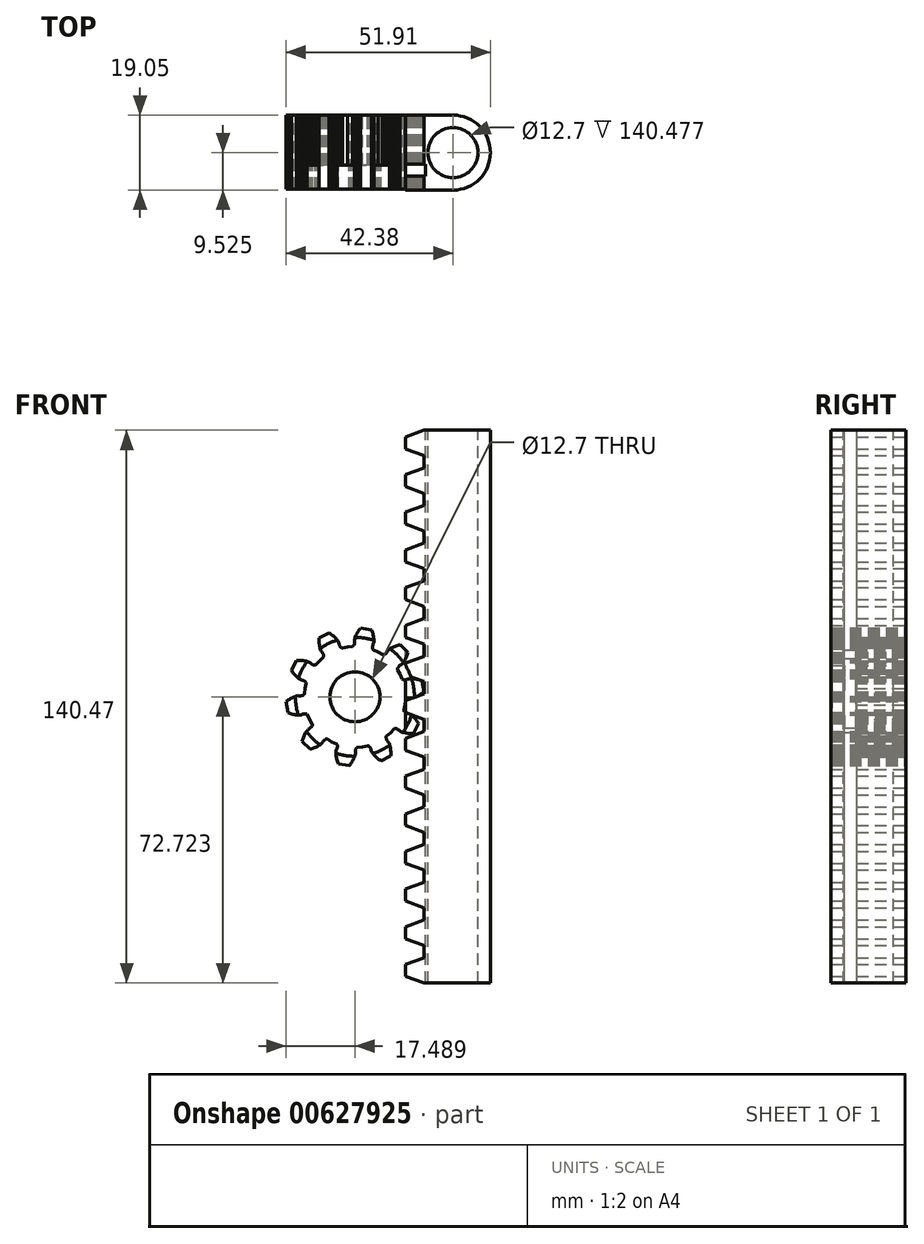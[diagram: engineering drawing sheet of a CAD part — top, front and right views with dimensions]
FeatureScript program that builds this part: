
annotation { "Feature Type Name" : "Feature", "Feature Type Description" : "" }
export const myFeature = defineFeature(function(context is Context, id is Id, definition is map)
    precondition{}
    {
        {
            var Q0;
            Q0=qCreatedBy(makeId("Front.planeOp"),FACE);
            var sketch = newSketch(context, id + "F0", { "sketchPlane" : qUnion([Q0])});
            skLineSegment(sketch, "E0", {"start": v(-42.72, 2.41) * mm, "end": v(-42.7, 2.18) * mm});
            skLineSegment(sketch, "E1", {"start": v(-42.7, 2.18) * mm, "end": v(-42.65, 2.08) * mm});
            skLineSegment(sketch, "E2", {"start": v(-42.65, 2.08) * mm, "end": v(-42.6, 2) * mm});
            skLineSegment(sketch, "E3", {"start": v(-42.6, 2) * mm, "end": v(-42.53, 1.93) * mm});
            skLineSegment(sketch, "E4", {"start": v(-42.53, 1.93) * mm, "end": v(-42.47, 1.88) * mm});
            skLineSegment(sketch, "E5", {"start": v(-42.47, 1.88) * mm, "end": v(-42.34, 1.78) * mm});
            skLineSegment(sketch, "E6", {"start": v(-42.34, 1.78) * mm, "end": v(-42.2, 1.7) * mm});
            skLineSegment(sketch, "E7", {"start": v(-42.2, 1.7) * mm, "end": v(-42.06, 1.63) * mm});
            skLineSegment(sketch, "E8", {"start": v(-42.06, 1.63) * mm, "end": v(-41.9, 1.57) * mm});
            skLineSegment(sketch, "E9", {"start": v(-41.9, 1.57) * mm, "end": v(-41.61, 1.48) * mm});
            skLineSegment(sketch, "E10", {"start": v(-41.61, 1.48) * mm, "end": v(-41.31, 1.38) * mm});
            skLineSegment(sketch, "E11", {"start": v(-41.31, 1.38) * mm, "end": v(-41.04, 1.22) * mm});
            skLineSegment(sketch, "E12", {"start": v(-41.04, 1.22) * mm, "end": v(-40.77, 1.04) * mm});
            skLineSegment(sketch, "E13", {"start": v(-40.77, 1.04) * mm, "end": v(-40.5, 0.83) * mm});
            skLineSegment(sketch, "E14", {"start": v(-40.5, 0.83) * mm, "end": v(-40.26, 0.6) * mm});
            skLineSegment(sketch, "E15", {"start": v(-40.26, 0.6) * mm, "end": v(-40.01, 0.35) * mm});
            skLineSegment(sketch, "E16", {"start": v(-40.01, 0.35) * mm, "end": v(-39.77, 0.1) * mm});
            skLineSegment(sketch, "E17", {"start": v(-39.77, 0.1) * mm, "end": v(-39.54, -0.19) * mm});
            skLineSegment(sketch, "E18", {"start": v(-39.54, -0.19) * mm, "end": v(-39.32, -0.48) * mm});
            skLineSegment(sketch, "E19", {"start": v(-39.32, -0.48) * mm, "end": v(-39.1, -0.79) * mm});
            skLineSegment(sketch, "E20", {"start": v(-39.1, -0.79) * mm, "end": v(-38.95, -1.03) * mm});
            skLineSegment(sketch, "E21", {"start": v(-38.95, -1.03) * mm, "end": v(-40.25, -3.53) * mm});
            skLineSegment(sketch, "E22", {"start": v(-40.25, -3.53) * mm, "end": v(-40.53, -3.54) * mm});
            skLineSegment(sketch, "E23", {"start": v(-40.53, -3.54) * mm, "end": v(-40.9, -3.55) * mm});
            skLineSegment(sketch, "E24", {"start": v(-40.9, -3.55) * mm, "end": v(-41.28, -3.53) * mm});
            skLineSegment(sketch, "E25", {"start": v(-41.28, -3.53) * mm, "end": v(-41.63, -3.5) * mm});
            skLineSegment(sketch, "E26", {"start": v(-41.63, -3.5) * mm, "end": v(-41.99, -3.46) * mm});
            skLineSegment(sketch, "E27", {"start": v(-41.99, -3.46) * mm, "end": v(-42.33, -3.4) * mm});
            skLineSegment(sketch, "E28", {"start": v(-42.33, -3.4) * mm, "end": v(-42.66, -3.33) * mm});
            skLineSegment(sketch, "E29", {"start": v(-42.66, -3.33) * mm, "end": v(-42.98, -3.24) * mm});
            skLineSegment(sketch, "E30", {"start": v(-42.98, -3.24) * mm, "end": v(-43.29, -3.13) * mm});
            skLineSegment(sketch, "E31", {"start": v(-43.29, -3.13) * mm, "end": v(-43.58, -3) * mm});
            skLineSegment(sketch, "E32", {"start": v(-43.58, -3) * mm, "end": v(-43.83, -2.8) * mm});
            skLineSegment(sketch, "E33", {"start": v(-43.83, -2.8) * mm, "end": v(-44.08, -2.62) * mm});
            skLineSegment(sketch, "E34", {"start": v(-44.08, -2.62) * mm, "end": v(-44.2, -2.53) * mm});
            skLineSegment(sketch, "E35", {"start": v(-44.2, -2.53) * mm, "end": v(-44.35, -2.45) * mm});
            skLineSegment(sketch, "E36", {"start": v(-44.35, -2.45) * mm, "end": v(-44.5, -2.39) * mm});
            skLineSegment(sketch, "E37", {"start": v(-44.5, -2.39) * mm, "end": v(-44.65, -2.34) * mm});
            skLineSegment(sketch, "E38", {"start": v(-44.65, -2.34) * mm, "end": v(-44.73, -2.32) * mm});
            skLineSegment(sketch, "E39", {"start": v(-44.73, -2.32) * mm, "end": v(-44.82, -2.3) * mm});
            skLineSegment(sketch, "E40", {"start": v(-44.82, -2.3) * mm, "end": v(-44.92, -2.3) * mm});
            skLineSegment(sketch, "E41", {"start": v(-44.92, -2.3) * mm, "end": v(-45.03, -2.32) * mm});
            skLineSegment(sketch, "E42", {"start": v(-45.03, -2.32) * mm, "end": v(-45.23, -2.44) * mm});
            skLineSegment(sketch, "E43", {"start": v(-45.23, -2.44) * mm, "end": v(-46.1, -3.38) * mm});
            skLineSegment(sketch, "E44", {"start": v(-46.1, -3.38) * mm, "end": v(-47.05, -4.24) * mm});
            skLineSegment(sketch, "E45", {"start": v(-47.05, -4.24) * mm, "end": v(-47.18, -4.44) * mm});
            skLineSegment(sketch, "E46", {"start": v(-47.18, -4.44) * mm, "end": v(-47.2, -4.55) * mm});
            skLineSegment(sketch, "E47", {"start": v(-47.2, -4.55) * mm, "end": v(-47.2, -4.65) * mm});
            skLineSegment(sketch, "E48", {"start": v(-47.2, -4.65) * mm, "end": v(-47.18, -4.74) * mm});
            skLineSegment(sketch, "E49", {"start": v(-47.18, -4.74) * mm, "end": v(-47.16, -4.82) * mm});
            skLineSegment(sketch, "E50", {"start": v(-47.16, -4.82) * mm, "end": v(-47.11, -4.98) * mm});
            skLineSegment(sketch, "E51", {"start": v(-47.11, -4.98) * mm, "end": v(-47.05, -5.13) * mm});
            skLineSegment(sketch, "E52", {"start": v(-47.05, -5.13) * mm, "end": v(-46.98, -5.26) * mm});
            skLineSegment(sketch, "E53", {"start": v(-46.98, -5.26) * mm, "end": v(-46.9, -5.4) * mm});
            skLineSegment(sketch, "E54", {"start": v(-46.9, -5.4) * mm, "end": v(-46.7, -5.65) * mm});
            skLineSegment(sketch, "E55", {"start": v(-46.7, -5.65) * mm, "end": v(-46.52, -5.9) * mm});
            skLineSegment(sketch, "E56", {"start": v(-46.52, -5.9) * mm, "end": v(-46.39, -6.2) * mm});
            skLineSegment(sketch, "E57", {"start": v(-46.39, -6.2) * mm, "end": v(-46.28, -6.5) * mm});
            skLineSegment(sketch, "E58", {"start": v(-46.28, -6.5) * mm, "end": v(-46.2, -6.82) * mm});
            skLineSegment(sketch, "E59", {"start": v(-46.2, -6.82) * mm, "end": v(-46.12, -7.15) * mm});
            skLineSegment(sketch, "E60", {"start": v(-46.12, -7.15) * mm, "end": v(-46.07, -7.5) * mm});
            skLineSegment(sketch, "E61", {"start": v(-46.07, -7.5) * mm, "end": v(-46.03, -7.85) * mm});
            skLineSegment(sketch, "E62", {"start": v(-46.03, -7.85) * mm, "end": v(-46, -8.2) * mm});
            skLineSegment(sketch, "E63", {"start": v(-46, -8.2) * mm, "end": v(-46, -8.58) * mm});
            skLineSegment(sketch, "E64", {"start": v(-46, -8.58) * mm, "end": v(-46.01, -8.95) * mm});
            skLineSegment(sketch, "E65", {"start": v(-46.01, -8.95) * mm, "end": v(-46.03, -9.24) * mm});
            skLineSegment(sketch, "E66", {"start": v(-46.03, -9.24) * mm, "end": v(-48.55, -10.5) * mm});
            skLineSegment(sketch, "E67", {"start": v(-48.55, -10.5) * mm, "end": v(-48.78, -10.34) * mm});
            skLineSegment(sketch, "E68", {"start": v(-48.78, -10.34) * mm, "end": v(-49.09, -10.12) * mm});
            skLineSegment(sketch, "E69", {"start": v(-49.09, -10.12) * mm, "end": v(-49.38, -9.9) * mm});
            skLineSegment(sketch, "E70", {"start": v(-49.38, -9.9) * mm, "end": v(-49.65, -9.67) * mm});
            skLineSegment(sketch, "E71", {"start": v(-49.65, -9.67) * mm, "end": v(-49.91, -9.42) * mm});
            skLineSegment(sketch, "E72", {"start": v(-49.91, -9.42) * mm, "end": v(-50.16, -9.18) * mm});
            skLineSegment(sketch, "E73", {"start": v(-50.16, -9.18) * mm, "end": v(-50.38, -8.92) * mm});
            skLineSegment(sketch, "E74", {"start": v(-50.38, -8.92) * mm, "end": v(-50.59, -8.66) * mm});
            skLineSegment(sketch, "E75", {"start": v(-50.59, -8.66) * mm, "end": v(-50.77, -8.39) * mm});
            skLineSegment(sketch, "E76", {"start": v(-50.77, -8.39) * mm, "end": v(-50.92, -8.1) * mm});
            skLineSegment(sketch, "E77", {"start": v(-50.92, -8.1) * mm, "end": v(-51.02, -7.8) * mm});
            skLineSegment(sketch, "E78", {"start": v(-51.02, -7.8) * mm, "end": v(-51.1, -7.51) * mm});
            skLineSegment(sketch, "E79", {"start": v(-51.1, -7.51) * mm, "end": v(-51.16, -7.36) * mm});
            skLineSegment(sketch, "E80", {"start": v(-51.16, -7.36) * mm, "end": v(-51.23, -7.22) * mm});
            skLineSegment(sketch, "E81", {"start": v(-51.23, -7.22) * mm, "end": v(-51.3, -7.08) * mm});
            skLineSegment(sketch, "E82", {"start": v(-51.3, -7.08) * mm, "end": v(-51.4, -6.95) * mm});
            skLineSegment(sketch, "E83", {"start": v(-51.4, -6.95) * mm, "end": v(-51.46, -6.88) * mm});
            skLineSegment(sketch, "E84", {"start": v(-51.46, -6.88) * mm, "end": v(-51.53, -6.82) * mm});
            skLineSegment(sketch, "E85", {"start": v(-51.53, -6.82) * mm, "end": v(-51.6, -6.76) * mm});
            skLineSegment(sketch, "E86", {"start": v(-51.6, -6.76) * mm, "end": v(-51.7, -6.7) * mm});
            skLineSegment(sketch, "E87", {"start": v(-51.7, -6.7) * mm, "end": v(-51.94, -6.69) * mm});
            skLineSegment(sketch, "E88", {"start": v(-51.94, -6.69) * mm, "end": v(-53.2, -6.94) * mm});
            skLineSegment(sketch, "E89", {"start": v(-53.2, -6.94) * mm, "end": v(-54.47, -7.07) * mm});
            skLineSegment(sketch, "E90", {"start": v(-54.47, -7.07) * mm, "end": v(-54.68, -7.16) * mm});
            skLineSegment(sketch, "E91", {"start": v(-54.68, -7.16) * mm, "end": v(-54.76, -7.24) * mm});
            skLineSegment(sketch, "E92", {"start": v(-54.76, -7.24) * mm, "end": v(-54.82, -7.32) * mm});
            skLineSegment(sketch, "E93", {"start": v(-54.82, -7.32) * mm, "end": v(-54.86, -7.4) * mm});
            skLineSegment(sketch, "E94", {"start": v(-54.86, -7.4) * mm, "end": v(-54.9, -7.48) * mm});
            skLineSegment(sketch, "E95", {"start": v(-54.9, -7.48) * mm, "end": v(-54.95, -7.64) * mm});
            skLineSegment(sketch, "E96", {"start": v(-54.95, -7.64) * mm, "end": v(-54.99, -7.8) * mm});
            skLineSegment(sketch, "E97", {"start": v(-54.99, -7.8) * mm, "end": v(-55, -7.95) * mm});
            skLineSegment(sketch, "E98", {"start": v(-55, -7.95) * mm, "end": v(-55.02, -8.1) * mm});
            skLineSegment(sketch, "E99", {"start": v(-55.02, -8.1) * mm, "end": v(-55.01, -8.42) * mm});
            skLineSegment(sketch, "E100", {"start": v(-55.01, -8.42) * mm, "end": v(-55.01, -8.73) * mm});
            skLineSegment(sketch, "E101", {"start": v(-55.01, -8.73) * mm, "end": v(-55.08, -9.04) * mm});
            skLineSegment(sketch, "E102", {"start": v(-55.08, -9.04) * mm, "end": v(-55.17, -9.36) * mm});
            skLineSegment(sketch, "E103", {"start": v(-55.17, -9.36) * mm, "end": v(-55.3, -9.67) * mm});
            skLineSegment(sketch, "E104", {"start": v(-55.3, -9.67) * mm, "end": v(-55.43, -9.98) * mm});
            skLineSegment(sketch, "E105", {"start": v(-55.43, -9.98) * mm, "end": v(-55.59, -10.29) * mm});
            skLineSegment(sketch, "E106", {"start": v(-55.59, -10.29) * mm, "end": v(-55.76, -10.6) * mm});
            skLineSegment(sketch, "E107", {"start": v(-55.76, -10.6) * mm, "end": v(-55.96, -10.9) * mm});
            skLineSegment(sketch, "E108", {"start": v(-55.96, -10.9) * mm, "end": v(-56.17, -11.2) * mm});
            skLineSegment(sketch, "E109", {"start": v(-56.17, -11.2) * mm, "end": v(-56.4, -11.5) * mm});
            skLineSegment(sketch, "E110", {"start": v(-56.4, -11.5) * mm, "end": v(-56.57, -11.72) * mm});
            skLineSegment(sketch, "E111", {"start": v(-56.57, -11.72) * mm, "end": v(-59.35, -11.26) * mm});
            skLineSegment(sketch, "E112", {"start": v(-59.35, -11.26) * mm, "end": v(-59.45, -11) * mm});
            skLineSegment(sketch, "E113", {"start": v(-59.45, -11) * mm, "end": v(-59.57, -10.64) * mm});
            skLineSegment(sketch, "E114", {"start": v(-59.57, -10.64) * mm, "end": v(-59.67, -10.29) * mm});
            skLineSegment(sketch, "E115", {"start": v(-59.67, -10.29) * mm, "end": v(-59.76, -9.93) * mm});
            skLineSegment(sketch, "E116", {"start": v(-59.76, -9.93) * mm, "end": v(-59.83, -9.59) * mm});
            skLineSegment(sketch, "E117", {"start": v(-59.83, -9.59) * mm, "end": v(-59.88, -9.24) * mm});
            skLineSegment(sketch, "E118", {"start": v(-59.88, -9.24) * mm, "end": v(-59.91, -8.9) * mm});
            skLineSegment(sketch, "E119", {"start": v(-59.91, -8.9) * mm, "end": v(-59.92, -8.57) * mm});
            skLineSegment(sketch, "E120", {"start": v(-59.92, -8.57) * mm, "end": v(-59.91, -8.25) * mm});
            skLineSegment(sketch, "E121", {"start": v(-59.91, -8.25) * mm, "end": v(-59.87, -7.93) * mm});
            skLineSegment(sketch, "E122", {"start": v(-59.87, -7.93) * mm, "end": v(-59.77, -7.63) * mm});
            skLineSegment(sketch, "E123", {"start": v(-59.77, -7.63) * mm, "end": v(-59.67, -7.34) * mm});
            skLineSegment(sketch, "E124", {"start": v(-59.67, -7.34) * mm, "end": v(-59.63, -7.19) * mm});
            skLineSegment(sketch, "E125", {"start": v(-59.63, -7.19) * mm, "end": v(-59.6, -7.03) * mm});
            skLineSegment(sketch, "E126", {"start": v(-59.6, -7.03) * mm, "end": v(-59.58, -6.87) * mm});
            skLineSegment(sketch, "E127", {"start": v(-59.58, -6.87) * mm, "end": v(-59.58, -6.7) * mm});
            skLineSegment(sketch, "E128", {"start": v(-59.58, -6.7) * mm, "end": v(-59.59, -6.62) * mm});
            skLineSegment(sketch, "E129", {"start": v(-59.59, -6.62) * mm, "end": v(-59.6, -6.53) * mm});
            skLineSegment(sketch, "E130", {"start": v(-59.6, -6.53) * mm, "end": v(-59.63, -6.44) * mm});
            skLineSegment(sketch, "E131", {"start": v(-59.63, -6.44) * mm, "end": v(-59.68, -6.34) * mm});
            skLineSegment(sketch, "E132", {"start": v(-59.68, -6.34) * mm, "end": v(-59.86, -6.18) * mm});
            skLineSegment(sketch, "E133", {"start": v(-59.86, -6.18) * mm, "end": v(-61.02, -5.65) * mm});
            skLineSegment(sketch, "E134", {"start": v(-61.02, -5.65) * mm, "end": v(-62.13, -5) * mm});
            skLineSegment(sketch, "E135", {"start": v(-62.13, -5) * mm, "end": v(-62.36, -4.95) * mm});
            skLineSegment(sketch, "E136", {"start": v(-62.36, -4.95) * mm, "end": v(-62.47, -4.97) * mm});
            skLineSegment(sketch, "E137", {"start": v(-62.47, -4.97) * mm, "end": v(-62.56, -5) * mm});
            skLineSegment(sketch, "E138", {"start": v(-62.56, -5) * mm, "end": v(-62.64, -5.04) * mm});
            skLineSegment(sketch, "E139", {"start": v(-62.64, -5.04) * mm, "end": v(-62.72, -5.08) * mm});
            skLineSegment(sketch, "E140", {"start": v(-62.72, -5.08) * mm, "end": v(-62.85, -5.18) * mm});
            skLineSegment(sketch, "E141", {"start": v(-62.85, -5.18) * mm, "end": v(-62.97, -5.28) * mm});
            skLineSegment(sketch, "E142", {"start": v(-62.97, -5.28) * mm, "end": v(-63.08, -5.4) * mm});
            skLineSegment(sketch, "E143", {"start": v(-63.08, -5.4) * mm, "end": v(-63.18, -5.52) * mm});
            skLineSegment(sketch, "E144", {"start": v(-63.18, -5.52) * mm, "end": v(-63.36, -5.77) * mm});
            skLineSegment(sketch, "E145", {"start": v(-63.36, -5.77) * mm, "end": v(-63.55, -6.03) * mm});
            skLineSegment(sketch, "E146", {"start": v(-63.55, -6.03) * mm, "end": v(-63.78, -6.24) * mm});
            skLineSegment(sketch, "E147", {"start": v(-63.78, -6.24) * mm, "end": v(-64.04, -6.44) * mm});
            skLineSegment(sketch, "E148", {"start": v(-64.04, -6.44) * mm, "end": v(-64.32, -6.62) * mm});
            skLineSegment(sketch, "E149", {"start": v(-64.32, -6.62) * mm, "end": v(-64.62, -6.8) * mm});
            skLineSegment(sketch, "E150", {"start": v(-64.62, -6.8) * mm, "end": v(-64.93, -6.95) * mm});
            skLineSegment(sketch, "E151", {"start": v(-64.93, -6.95) * mm, "end": v(-65.25, -7.1) * mm});
            skLineSegment(sketch, "E152", {"start": v(-65.25, -7.1) * mm, "end": v(-65.58, -7.23) * mm});
            skLineSegment(sketch, "E153", {"start": v(-65.58, -7.23) * mm, "end": v(-65.93, -7.35) * mm});
            skLineSegment(sketch, "E154", {"start": v(-65.93, -7.35) * mm, "end": v(-66.3, -7.46) * mm});
            skLineSegment(sketch, "E155", {"start": v(-66.3, -7.46) * mm, "end": v(-66.57, -7.53) * mm});
            skLineSegment(sketch, "E156", {"start": v(-66.57, -7.53) * mm, "end": v(-68.55, -5.52) * mm});
            skLineSegment(sketch, "E157", {"start": v(-68.55, -5.52) * mm, "end": v(-68.47, -5.25) * mm});
            skLineSegment(sketch, "E158", {"start": v(-68.47, -5.25) * mm, "end": v(-68.36, -4.9) * mm});
            skLineSegment(sketch, "E159", {"start": v(-68.36, -4.9) * mm, "end": v(-68.23, -4.55) * mm});
            skLineSegment(sketch, "E160", {"start": v(-68.23, -4.55) * mm, "end": v(-68.1, -4.21) * mm});
            skLineSegment(sketch, "E161", {"start": v(-68.1, -4.21) * mm, "end": v(-67.95, -3.9) * mm});
            skLineSegment(sketch, "E162", {"start": v(-67.95, -3.9) * mm, "end": v(-67.79, -3.58) * mm});
            skLineSegment(sketch, "E163", {"start": v(-67.79, -3.58) * mm, "end": v(-67.61, -3.3) * mm});
            skLineSegment(sketch, "E164", {"start": v(-67.61, -3.3) * mm, "end": v(-67.43, -3.01) * mm});
            skLineSegment(sketch, "E165", {"start": v(-67.43, -3.01) * mm, "end": v(-67.23, -2.76) * mm});
            skLineSegment(sketch, "E166", {"start": v(-67.23, -2.76) * mm, "end": v(-67, -2.52) * mm});
            skLineSegment(sketch, "E167", {"start": v(-67, -2.52) * mm, "end": v(-66.75, -2.34) * mm});
            skLineSegment(sketch, "E168", {"start": v(-66.75, -2.34) * mm, "end": v(-66.5, -2.17) * mm});
            skLineSegment(sketch, "E169", {"start": v(-66.5, -2.17) * mm, "end": v(-66.37, -2.07) * mm});
            skLineSegment(sketch, "E170", {"start": v(-66.37, -2.07) * mm, "end": v(-66.26, -1.96) * mm});
            skLineSegment(sketch, "E171", {"start": v(-66.26, -1.96) * mm, "end": v(-66.15, -1.84) * mm});
            skLineSegment(sketch, "E172", {"start": v(-66.15, -1.84) * mm, "end": v(-66.05, -1.7) * mm});
            skLineSegment(sketch, "E173", {"start": v(-66.05, -1.7) * mm, "end": v(-66, -1.63) * mm});
            skLineSegment(sketch, "E174", {"start": v(-66, -1.63) * mm, "end": v(-65.97, -1.55) * mm});
            skLineSegment(sketch, "E175", {"start": v(-65.97, -1.55) * mm, "end": v(-65.94, -1.46) * mm});
            skLineSegment(sketch, "E176", {"start": v(-65.94, -1.46) * mm, "end": v(-65.92, -1.35) * mm});
            skLineSegment(sketch, "E177", {"start": v(-65.92, -1.35) * mm, "end": v(-65.97, -1.12) * mm});
            skLineSegment(sketch, "E178", {"start": v(-65.97, -1.12) * mm, "end": v(-66.6, 0) * mm});
            skLineSegment(sketch, "E179", {"start": v(-66.6, 0) * mm, "end": v(-67.12, 1.17) * mm});
            skLineSegment(sketch, "E180", {"start": v(-67.12, 1.17) * mm, "end": v(-67.27, 1.35) * mm});
            skLineSegment(sketch, "E181", {"start": v(-67.27, 1.35) * mm, "end": v(-67.37, 1.4) * mm});
            skLineSegment(sketch, "E182", {"start": v(-67.37, 1.4) * mm, "end": v(-67.46, 1.43) * mm});
            skLineSegment(sketch, "E183", {"start": v(-67.46, 1.43) * mm, "end": v(-67.55, 1.44) * mm});
            skLineSegment(sketch, "E184", {"start": v(-67.55, 1.44) * mm, "end": v(-67.64, 1.45) * mm});
            skLineSegment(sketch, "E185", {"start": v(-67.64, 1.45) * mm, "end": v(-67.8, 1.45) * mm});
            skLineSegment(sketch, "E186", {"start": v(-67.8, 1.45) * mm, "end": v(-67.96, 1.44) * mm});
            skLineSegment(sketch, "E187", {"start": v(-67.96, 1.44) * mm, "end": v(-68.12, 1.41) * mm});
            skLineSegment(sketch, "E188", {"start": v(-68.12, 1.41) * mm, "end": v(-68.27, 1.37) * mm});
            skLineSegment(sketch, "E189", {"start": v(-68.27, 1.37) * mm, "end": v(-68.57, 1.27) * mm});
            skLineSegment(sketch, "E190", {"start": v(-68.57, 1.27) * mm, "end": v(-68.86, 1.18) * mm});
            skLineSegment(sketch, "E191", {"start": v(-68.86, 1.18) * mm, "end": v(-69.18, 1.14) * mm});
            skLineSegment(sketch, "E192", {"start": v(-69.18, 1.14) * mm, "end": v(-69.5, 1.13) * mm});
            skLineSegment(sketch, "E193", {"start": v(-69.5, 1.13) * mm, "end": v(-69.84, 1.15) * mm});
            skLineSegment(sketch, "E194", {"start": v(-69.84, 1.15) * mm, "end": v(-70.18, 1.18) * mm});
            skLineSegment(sketch, "E195", {"start": v(-70.18, 1.18) * mm, "end": v(-70.52, 1.24) * mm});
            skLineSegment(sketch, "E196", {"start": v(-70.52, 1.24) * mm, "end": v(-70.87, 1.31) * mm});
            skLineSegment(sketch, "E197", {"start": v(-70.87, 1.31) * mm, "end": v(-71.22, 1.4) * mm});
            skLineSegment(sketch, "E198", {"start": v(-71.22, 1.4) * mm, "end": v(-71.57, 1.5) * mm});
            skLineSegment(sketch, "E199", {"start": v(-71.57, 1.5) * mm, "end": v(-71.92, 1.63) * mm});
            skLineSegment(sketch, "E200", {"start": v(-71.92, 1.63) * mm, "end": v(-72.19, 1.74) * mm});
            skLineSegment(sketch, "E201", {"start": v(-72.19, 1.74) * mm, "end": v(-72.61, 4.52) * mm});
            skLineSegment(sketch, "E202", {"start": v(-72.61, 4.52) * mm, "end": v(-72.39, 4.7) * mm});
            skLineSegment(sketch, "E203", {"start": v(-72.39, 4.7) * mm, "end": v(-72.09, 4.92) * mm});
            skLineSegment(sketch, "E204", {"start": v(-72.09, 4.92) * mm, "end": v(-71.78, 5.13) * mm});
            skLineSegment(sketch, "E205", {"start": v(-71.78, 5.13) * mm, "end": v(-71.48, 5.32) * mm});
            skLineSegment(sketch, "E206", {"start": v(-71.48, 5.32) * mm, "end": v(-71.17, 5.49) * mm});
            skLineSegment(sketch, "E207", {"start": v(-71.17, 5.49) * mm, "end": v(-70.86, 5.64) * mm});
            skLineSegment(sketch, "E208", {"start": v(-70.86, 5.64) * mm, "end": v(-70.54, 5.78) * mm});
            skLineSegment(sketch, "E209", {"start": v(-70.54, 5.78) * mm, "end": v(-70.23, 5.9) * mm});
            skLineSegment(sketch, "E210", {"start": v(-70.23, 5.9) * mm, "end": v(-69.92, 5.98) * mm});
            skLineSegment(sketch, "E211", {"start": v(-69.92, 5.98) * mm, "end": v(-69.6, 6.04) * mm});
            skLineSegment(sketch, "E212", {"start": v(-69.6, 6.04) * mm, "end": v(-69.29, 6.04) * mm});
            skLineSegment(sketch, "E213", {"start": v(-69.29, 6.04) * mm, "end": v(-68.98, 6.03) * mm});
            skLineSegment(sketch, "E214", {"start": v(-68.98, 6.03) * mm, "end": v(-68.82, 6.04) * mm});
            skLineSegment(sketch, "E215", {"start": v(-68.82, 6.04) * mm, "end": v(-68.66, 6.06) * mm});
            skLineSegment(sketch, "E216", {"start": v(-68.66, 6.06) * mm, "end": v(-68.5, 6.1) * mm});
            skLineSegment(sketch, "E217", {"start": v(-68.5, 6.1) * mm, "end": v(-68.35, 6.14) * mm});
            skLineSegment(sketch, "E218", {"start": v(-68.35, 6.14) * mm, "end": v(-68.27, 6.18) * mm});
            skLineSegment(sketch, "E219", {"start": v(-68.27, 6.18) * mm, "end": v(-68.2, 6.22) * mm});
            skLineSegment(sketch, "E220", {"start": v(-68.2, 6.22) * mm, "end": v(-68.1, 6.27) * mm});
            skLineSegment(sketch, "E221", {"start": v(-68.1, 6.27) * mm, "end": v(-68.03, 6.35) * mm});
            skLineSegment(sketch, "E222", {"start": v(-68.03, 6.35) * mm, "end": v(-67.94, 6.57) * mm});
            skLineSegment(sketch, "E223", {"start": v(-67.94, 6.57) * mm, "end": v(-67.8, 7.84) * mm});
            skLineSegment(sketch, "E224", {"start": v(-67.8, 7.84) * mm, "end": v(-67.52, 9.1) * mm});
            skLineSegment(sketch, "E225", {"start": v(-67.52, 9.1) * mm, "end": v(-67.54, 9.33) * mm});
            skLineSegment(sketch, "E226", {"start": v(-67.54, 9.33) * mm, "end": v(-67.6, 9.43) * mm});
            skLineSegment(sketch, "E227", {"start": v(-67.6, 9.43) * mm, "end": v(-67.65, 9.5) * mm});
            skLineSegment(sketch, "E228", {"start": v(-67.65, 9.5) * mm, "end": v(-67.7, 9.57) * mm});
            skLineSegment(sketch, "E229", {"start": v(-67.7, 9.57) * mm, "end": v(-67.77, 9.63) * mm});
            skLineSegment(sketch, "E230", {"start": v(-67.77, 9.63) * mm, "end": v(-67.9, 9.73) * mm});
            skLineSegment(sketch, "E231", {"start": v(-67.9, 9.73) * mm, "end": v(-68.05, 9.81) * mm});
            skLineSegment(sketch, "E232", {"start": v(-68.05, 9.81) * mm, "end": v(-68.19, 9.88) * mm});
            skLineSegment(sketch, "E233", {"start": v(-68.19, 9.88) * mm, "end": v(-68.33, 9.94) * mm});
            skLineSegment(sketch, "E234", {"start": v(-68.33, 9.94) * mm, "end": v(-68.63, 10.03) * mm});
            skLineSegment(sketch, "E235", {"start": v(-68.63, 10.03) * mm, "end": v(-68.93, 10.13) * mm});
            skLineSegment(sketch, "E236", {"start": v(-68.93, 10.13) * mm, "end": v(-69.2, 10.28) * mm});
            skLineSegment(sketch, "E237", {"start": v(-69.2, 10.28) * mm, "end": v(-69.48, 10.47) * mm});
            skLineSegment(sketch, "E238", {"start": v(-69.48, 10.47) * mm, "end": v(-69.74, 10.68) * mm});
            skLineSegment(sketch, "E239", {"start": v(-69.74, 10.68) * mm, "end": v(-69.99, 10.9) * mm});
            skLineSegment(sketch, "E240", {"start": v(-69.99, 10.9) * mm, "end": v(-70.23, 11.15) * mm});
            skLineSegment(sketch, "E241", {"start": v(-70.23, 11.15) * mm, "end": v(-70.47, 11.41) * mm});
            skLineSegment(sketch, "E242", {"start": v(-70.47, 11.41) * mm, "end": v(-70.7, 11.7) * mm});
            skLineSegment(sketch, "E243", {"start": v(-70.7, 11.7) * mm, "end": v(-70.92, 11.99) * mm});
            skLineSegment(sketch, "E244", {"start": v(-70.92, 11.99) * mm, "end": v(-71.13, 12.3) * mm});
            skLineSegment(sketch, "E245", {"start": v(-71.13, 12.3) * mm, "end": v(-71.29, 12.53) * mm});
            skLineSegment(sketch, "E246", {"start": v(-71.29, 12.53) * mm, "end": v(-70, 15.04) * mm});
            skLineSegment(sketch, "E247", {"start": v(-70, 15.04) * mm, "end": v(-69.7, 15.05) * mm});
            skLineSegment(sketch, "E248", {"start": v(-69.7, 15.05) * mm, "end": v(-69.34, 15.05) * mm});
            skLineSegment(sketch, "E249", {"start": v(-69.34, 15.05) * mm, "end": v(-68.97, 15.04) * mm});
            skLineSegment(sketch, "E250", {"start": v(-68.97, 15.04) * mm, "end": v(-68.6, 15.01) * mm});
            skLineSegment(sketch, "E251", {"start": v(-68.6, 15.01) * mm, "end": v(-68.26, 14.97) * mm});
            skLineSegment(sketch, "E252", {"start": v(-68.26, 14.97) * mm, "end": v(-67.92, 14.91) * mm});
            skLineSegment(sketch, "E253", {"start": v(-67.92, 14.91) * mm, "end": v(-67.58, 14.84) * mm});
            skLineSegment(sketch, "E254", {"start": v(-67.58, 14.84) * mm, "end": v(-67.26, 14.75) * mm});
            skLineSegment(sketch, "E255", {"start": v(-67.26, 14.75) * mm, "end": v(-66.96, 14.63) * mm});
            skLineSegment(sketch, "E256", {"start": v(-66.96, 14.63) * mm, "end": v(-66.67, 14.5) * mm});
            skLineSegment(sketch, "E257", {"start": v(-66.67, 14.5) * mm, "end": v(-66.42, 14.31) * mm});
            skLineSegment(sketch, "E258", {"start": v(-66.42, 14.31) * mm, "end": v(-66.17, 14.12) * mm});
            skLineSegment(sketch, "E259", {"start": v(-66.17, 14.12) * mm, "end": v(-66.04, 14.04) * mm});
            skLineSegment(sketch, "E260", {"start": v(-66.04, 14.04) * mm, "end": v(-65.9, 13.96) * mm});
            skLineSegment(sketch, "E261", {"start": v(-65.9, 13.96) * mm, "end": v(-65.75, 13.9) * mm});
            skLineSegment(sketch, "E262", {"start": v(-65.75, 13.9) * mm, "end": v(-65.6, 13.84) * mm});
            skLineSegment(sketch, "E263", {"start": v(-65.6, 13.84) * mm, "end": v(-65.51, 13.82) * mm});
            skLineSegment(sketch, "E264", {"start": v(-65.51, 13.82) * mm, "end": v(-65.42, 13.81) * mm});
            skLineSegment(sketch, "E265", {"start": v(-65.42, 13.81) * mm, "end": v(-65.32, 13.8) * mm});
            skLineSegment(sketch, "E266", {"start": v(-65.32, 13.8) * mm, "end": v(-65.2, 13.83) * mm});
            skLineSegment(sketch, "E267", {"start": v(-65.2, 13.83) * mm, "end": v(-65.01, 13.95) * mm});
            skLineSegment(sketch, "E268", {"start": v(-65.01, 13.95) * mm, "end": v(-64.15, 14.9) * mm});
            skLineSegment(sketch, "E269", {"start": v(-64.15, 14.9) * mm, "end": v(-63.19, 15.75) * mm});
            skLineSegment(sketch, "E270", {"start": v(-63.19, 15.75) * mm, "end": v(-63.07, 15.94) * mm});
            skLineSegment(sketch, "E271", {"start": v(-63.07, 15.94) * mm, "end": v(-63.05, 16.05) * mm});
            skLineSegment(sketch, "E272", {"start": v(-63.05, 16.05) * mm, "end": v(-63.05, 16.15) * mm});
            skLineSegment(sketch, "E273", {"start": v(-63.05, 16.15) * mm, "end": v(-63.06, 16.24) * mm});
            skLineSegment(sketch, "E274", {"start": v(-63.06, 16.24) * mm, "end": v(-63.08, 16.33) * mm});
            skLineSegment(sketch, "E275", {"start": v(-63.08, 16.33) * mm, "end": v(-63.13, 16.48) * mm});
            skLineSegment(sketch, "E276", {"start": v(-63.13, 16.48) * mm, "end": v(-63.2, 16.63) * mm});
            skLineSegment(sketch, "E277", {"start": v(-63.2, 16.63) * mm, "end": v(-63.27, 16.77) * mm});
            skLineSegment(sketch, "E278", {"start": v(-63.27, 16.77) * mm, "end": v(-63.35, 16.9) * mm});
            skLineSegment(sketch, "E279", {"start": v(-63.35, 16.9) * mm, "end": v(-63.54, 17.15) * mm});
            skLineSegment(sketch, "E280", {"start": v(-63.54, 17.15) * mm, "end": v(-63.72, 17.4) * mm});
            skLineSegment(sketch, "E281", {"start": v(-63.72, 17.4) * mm, "end": v(-63.85, 17.7) * mm});
            skLineSegment(sketch, "E282", {"start": v(-63.85, 17.7) * mm, "end": v(-63.96, 18) * mm});
            skLineSegment(sketch, "E283", {"start": v(-63.96, 18) * mm, "end": v(-64.05, 18.33) * mm});
            skLineSegment(sketch, "E284", {"start": v(-64.05, 18.33) * mm, "end": v(-64.12, 18.66) * mm});
            skLineSegment(sketch, "E285", {"start": v(-64.12, 18.66) * mm, "end": v(-64.17, 19) * mm});
            skLineSegment(sketch, "E286", {"start": v(-64.17, 19) * mm, "end": v(-64.21, 19.36) * mm});
            skLineSegment(sketch, "E287", {"start": v(-64.21, 19.36) * mm, "end": v(-64.23, 19.72) * mm});
            skLineSegment(sketch, "E288", {"start": v(-64.23, 19.72) * mm, "end": v(-64.24, 20.08) * mm});
            skLineSegment(sketch, "E289", {"start": v(-64.24, 20.08) * mm, "end": v(-64.23, 20.46) * mm});
            skLineSegment(sketch, "E290", {"start": v(-64.23, 20.46) * mm, "end": v(-64.22, 20.74) * mm});
            skLineSegment(sketch, "E291", {"start": v(-64.22, 20.74) * mm, "end": v(-61.7, 22) * mm});
            skLineSegment(sketch, "E292", {"start": v(-61.7, 22) * mm, "end": v(-61.46, 21.85) * mm});
            skLineSegment(sketch, "E293", {"start": v(-61.46, 21.85) * mm, "end": v(-61.16, 21.63) * mm});
            skLineSegment(sketch, "E294", {"start": v(-61.16, 21.63) * mm, "end": v(-60.86, 21.4) * mm});
            skLineSegment(sketch, "E295", {"start": v(-60.86, 21.4) * mm, "end": v(-60.59, 21.17) * mm});
            skLineSegment(sketch, "E296", {"start": v(-60.59, 21.17) * mm, "end": v(-60.33, 20.93) * mm});
            skLineSegment(sketch, "E297", {"start": v(-60.33, 20.93) * mm, "end": v(-60.09, 20.68) * mm});
            skLineSegment(sketch, "E298", {"start": v(-60.09, 20.68) * mm, "end": v(-59.86, 20.43) * mm});
            skLineSegment(sketch, "E299", {"start": v(-59.86, 20.43) * mm, "end": v(-59.66, 20.17) * mm});
            skLineSegment(sketch, "E300", {"start": v(-59.66, 20.17) * mm, "end": v(-59.48, 19.9) * mm});
            skLineSegment(sketch, "E301", {"start": v(-59.48, 19.9) * mm, "end": v(-59.32, 19.61) * mm});
            skLineSegment(sketch, "E302", {"start": v(-59.32, 19.61) * mm, "end": v(-59.23, 19.32) * mm});
            skLineSegment(sketch, "E303", {"start": v(-59.23, 19.32) * mm, "end": v(-59.14, 19.02) * mm});
            skLineSegment(sketch, "E304", {"start": v(-59.14, 19.02) * mm, "end": v(-59.08, 18.87) * mm});
            skLineSegment(sketch, "E305", {"start": v(-59.08, 18.87) * mm, "end": v(-59.02, 18.73) * mm});
            skLineSegment(sketch, "E306", {"start": v(-59.02, 18.73) * mm, "end": v(-58.94, 18.59) * mm});
            skLineSegment(sketch, "E307", {"start": v(-58.94, 18.59) * mm, "end": v(-58.84, 18.45) * mm});
            skLineSegment(sketch, "E308", {"start": v(-58.84, 18.45) * mm, "end": v(-58.78, 18.39) * mm});
            skLineSegment(sketch, "E309", {"start": v(-58.78, 18.39) * mm, "end": v(-58.72, 18.33) * mm});
            skLineSegment(sketch, "E310", {"start": v(-58.72, 18.33) * mm, "end": v(-58.64, 18.27) * mm});
            skLineSegment(sketch, "E311", {"start": v(-58.64, 18.27) * mm, "end": v(-58.54, 18.21) * mm});
            skLineSegment(sketch, "E312", {"start": v(-58.54, 18.21) * mm, "end": v(-58.3, 18.2) * mm});
            skLineSegment(sketch, "E313", {"start": v(-58.3, 18.2) * mm, "end": v(-57.05, 18.45) * mm});
            skLineSegment(sketch, "E314", {"start": v(-57.05, 18.45) * mm, "end": v(-55.77, 18.58) * mm});
            skLineSegment(sketch, "E315", {"start": v(-55.77, 18.58) * mm, "end": v(-55.56, 18.67) * mm});
            skLineSegment(sketch, "E316", {"start": v(-55.56, 18.67) * mm, "end": v(-55.48, 18.75) * mm});
            skLineSegment(sketch, "E317", {"start": v(-55.48, 18.75) * mm, "end": v(-55.42, 18.83) * mm});
            skLineSegment(sketch, "E318", {"start": v(-55.42, 18.83) * mm, "end": v(-55.38, 18.9) * mm});
            skLineSegment(sketch, "E319", {"start": v(-55.38, 18.9) * mm, "end": v(-55.34, 18.98) * mm});
            skLineSegment(sketch, "E320", {"start": v(-55.34, 18.98) * mm, "end": v(-55.3, 19.14) * mm});
            skLineSegment(sketch, "E321", {"start": v(-55.3, 19.14) * mm, "end": v(-55.26, 19.3) * mm});
            skLineSegment(sketch, "E322", {"start": v(-55.26, 19.3) * mm, "end": v(-55.24, 19.45) * mm});
            skLineSegment(sketch, "E323", {"start": v(-55.24, 19.45) * mm, "end": v(-55.22, 19.61) * mm});
            skLineSegment(sketch, "E324", {"start": v(-55.22, 19.61) * mm, "end": v(-55.23, 19.92) * mm});
            skLineSegment(sketch, "E325", {"start": v(-55.23, 19.92) * mm, "end": v(-55.23, 20.24) * mm});
            skLineSegment(sketch, "E326", {"start": v(-55.23, 20.24) * mm, "end": v(-55.16, 20.55) * mm});
            skLineSegment(sketch, "E327", {"start": v(-55.16, 20.55) * mm, "end": v(-55.07, 20.86) * mm});
            skLineSegment(sketch, "E328", {"start": v(-55.07, 20.86) * mm, "end": v(-54.95, 21.17) * mm});
            skLineSegment(sketch, "E329", {"start": v(-54.95, 21.17) * mm, "end": v(-54.81, 21.48) * mm});
            skLineSegment(sketch, "E330", {"start": v(-54.81, 21.48) * mm, "end": v(-54.66, 21.8) * mm});
            skLineSegment(sketch, "E331", {"start": v(-54.66, 21.8) * mm, "end": v(-54.48, 22.1) * mm});
            skLineSegment(sketch, "E332", {"start": v(-54.48, 22.1) * mm, "end": v(-54.29, 22.4) * mm});
            skLineSegment(sketch, "E333", {"start": v(-54.29, 22.4) * mm, "end": v(-54.08, 22.7) * mm});
            skLineSegment(sketch, "E334", {"start": v(-54.08, 22.7) * mm, "end": v(-53.85, 23) * mm});
            skLineSegment(sketch, "E335", {"start": v(-53.85, 23) * mm, "end": v(-53.67, 23.22) * mm});
            skLineSegment(sketch, "E336", {"start": v(-53.67, 23.22) * mm, "end": v(-50.89, 22.77) * mm});
            skLineSegment(sketch, "E337", {"start": v(-50.89, 22.77) * mm, "end": v(-50.79, 22.5) * mm});
            skLineSegment(sketch, "E338", {"start": v(-50.79, 22.5) * mm, "end": v(-50.67, 22.14) * mm});
            skLineSegment(sketch, "E339", {"start": v(-50.67, 22.14) * mm, "end": v(-50.57, 21.8) * mm});
            skLineSegment(sketch, "E340", {"start": v(-50.57, 21.8) * mm, "end": v(-50.48, 21.44) * mm});
            skLineSegment(sketch, "E341", {"start": v(-50.48, 21.44) * mm, "end": v(-50.41, 21.1) * mm});
            skLineSegment(sketch, "E342", {"start": v(-50.41, 21.1) * mm, "end": v(-50.36, 20.75) * mm});
            skLineSegment(sketch, "E343", {"start": v(-50.36, 20.75) * mm, "end": v(-50.33, 20.41) * mm});
            skLineSegment(sketch, "E344", {"start": v(-50.33, 20.41) * mm, "end": v(-50.32, 20.08) * mm});
            skLineSegment(sketch, "E345", {"start": v(-50.32, 20.08) * mm, "end": v(-50.33, 19.75) * mm});
            skLineSegment(sketch, "E346", {"start": v(-50.33, 19.75) * mm, "end": v(-50.37, 19.44) * mm});
            skLineSegment(sketch, "E347", {"start": v(-50.37, 19.44) * mm, "end": v(-50.47, 19.14) * mm});
            skLineSegment(sketch, "E348", {"start": v(-50.47, 19.14) * mm, "end": v(-50.58, 18.85) * mm});
            skLineSegment(sketch, "E349", {"start": v(-50.58, 18.85) * mm, "end": v(-50.62, 18.7) * mm});
            skLineSegment(sketch, "E350", {"start": v(-50.62, 18.7) * mm, "end": v(-50.65, 18.54) * mm});
            skLineSegment(sketch, "E351", {"start": v(-50.65, 18.54) * mm, "end": v(-50.66, 18.38) * mm});
            skLineSegment(sketch, "E352", {"start": v(-50.66, 18.38) * mm, "end": v(-50.66, 18.21) * mm});
            skLineSegment(sketch, "E353", {"start": v(-50.66, 18.21) * mm, "end": v(-50.66, 18.13) * mm});
            skLineSegment(sketch, "E354", {"start": v(-50.66, 18.13) * mm, "end": v(-50.64, 18.04) * mm});
            skLineSegment(sketch, "E355", {"start": v(-50.64, 18.04) * mm, "end": v(-50.61, 17.94) * mm});
            skLineSegment(sketch, "E356", {"start": v(-50.61, 17.94) * mm, "end": v(-50.56, 17.84) * mm});
            skLineSegment(sketch, "E357", {"start": v(-50.56, 17.84) * mm, "end": v(-50.39, 17.7) * mm});
            skLineSegment(sketch, "E358", {"start": v(-50.39, 17.7) * mm, "end": v(-49.22, 17.16) * mm});
            skLineSegment(sketch, "E359", {"start": v(-49.22, 17.16) * mm, "end": v(-48.11, 16.51) * mm});
            skLineSegment(sketch, "E360", {"start": v(-48.11, 16.51) * mm, "end": v(-47.89, 16.46) * mm});
            skLineSegment(sketch, "E361", {"start": v(-47.89, 16.46) * mm, "end": v(-47.77, 16.48) * mm});
            skLineSegment(sketch, "E362", {"start": v(-47.77, 16.48) * mm, "end": v(-47.68, 16.5) * mm});
            skLineSegment(sketch, "E363", {"start": v(-47.68, 16.5) * mm, "end": v(-47.6, 16.55) * mm});
            skLineSegment(sketch, "E364", {"start": v(-47.6, 16.55) * mm, "end": v(-47.52, 16.59) * mm});
            skLineSegment(sketch, "E365", {"start": v(-47.52, 16.59) * mm, "end": v(-47.39, 16.68) * mm});
            skLineSegment(sketch, "E366", {"start": v(-47.39, 16.68) * mm, "end": v(-47.27, 16.8) * mm});
            skLineSegment(sketch, "E367", {"start": v(-47.27, 16.8) * mm, "end": v(-47.16, 16.9) * mm});
            skLineSegment(sketch, "E368", {"start": v(-47.16, 16.9) * mm, "end": v(-47.06, 17.03) * mm});
            skLineSegment(sketch, "E369", {"start": v(-47.06, 17.03) * mm, "end": v(-46.88, 17.28) * mm});
            skLineSegment(sketch, "E370", {"start": v(-46.88, 17.28) * mm, "end": v(-46.7, 17.53) * mm});
            skLineSegment(sketch, "E371", {"start": v(-46.7, 17.53) * mm, "end": v(-46.46, 17.75) * mm});
            skLineSegment(sketch, "E372", {"start": v(-46.46, 17.75) * mm, "end": v(-46.2, 17.95) * mm});
            skLineSegment(sketch, "E373", {"start": v(-46.2, 17.95) * mm, "end": v(-45.92, 18.13) * mm});
            skLineSegment(sketch, "E374", {"start": v(-45.92, 18.13) * mm, "end": v(-45.63, 18.3) * mm});
            skLineSegment(sketch, "E375", {"start": v(-45.63, 18.3) * mm, "end": v(-45.32, 18.46) * mm});
            skLineSegment(sketch, "E376", {"start": v(-45.32, 18.46) * mm, "end": v(-45, 18.6) * mm});
            skLineSegment(sketch, "E377", {"start": v(-45, 18.6) * mm, "end": v(-44.66, 18.73) * mm});
            skLineSegment(sketch, "E378", {"start": v(-44.66, 18.73) * mm, "end": v(-44.31, 18.85) * mm});
            skLineSegment(sketch, "E379", {"start": v(-44.31, 18.85) * mm, "end": v(-43.95, 18.96) * mm});
            skLineSegment(sketch, "E380", {"start": v(-43.95, 18.96) * mm, "end": v(-43.68, 19.03) * mm});
            skLineSegment(sketch, "E381", {"start": v(-43.68, 19.03) * mm, "end": v(-41.7, 17.03) * mm});
            skLineSegment(sketch, "E382", {"start": v(-41.7, 17.03) * mm, "end": v(-41.77, 16.75) * mm});
            skLineSegment(sketch, "E383", {"start": v(-41.77, 16.75) * mm, "end": v(-41.89, 16.4) * mm});
            skLineSegment(sketch, "E384", {"start": v(-41.89, 16.4) * mm, "end": v(-42.01, 16.05) * mm});
            skLineSegment(sketch, "E385", {"start": v(-42.01, 16.05) * mm, "end": v(-42.15, 15.72) * mm});
            skLineSegment(sketch, "E386", {"start": v(-42.15, 15.72) * mm, "end": v(-42.3, 15.4) * mm});
            skLineSegment(sketch, "E387", {"start": v(-42.3, 15.4) * mm, "end": v(-42.46, 15.09) * mm});
            skLineSegment(sketch, "E388", {"start": v(-42.46, 15.09) * mm, "end": v(-42.63, 14.8) * mm});
            skLineSegment(sketch, "E389", {"start": v(-42.63, 14.8) * mm, "end": v(-42.82, 14.52) * mm});
            skLineSegment(sketch, "E390", {"start": v(-42.82, 14.52) * mm, "end": v(-43.02, 14.26) * mm});
            skLineSegment(sketch, "E391", {"start": v(-43.02, 14.26) * mm, "end": v(-43.24, 14.03) * mm});
            skLineSegment(sketch, "E392", {"start": v(-43.24, 14.03) * mm, "end": v(-43.5, 13.85) * mm});
            skLineSegment(sketch, "E393", {"start": v(-43.5, 13.85) * mm, "end": v(-43.75, 13.67) * mm});
            skLineSegment(sketch, "E394", {"start": v(-43.75, 13.67) * mm, "end": v(-43.87, 13.57) * mm});
            skLineSegment(sketch, "E395", {"start": v(-43.87, 13.57) * mm, "end": v(-43.99, 13.47) * mm});
            skLineSegment(sketch, "E396", {"start": v(-43.99, 13.47) * mm, "end": v(-44.1, 13.35) * mm});
            skLineSegment(sketch, "E397", {"start": v(-44.1, 13.35) * mm, "end": v(-44.2, 13.21) * mm});
            skLineSegment(sketch, "E398", {"start": v(-44.2, 13.21) * mm, "end": v(-44.24, 13.14) * mm});
            skLineSegment(sketch, "E399", {"start": v(-44.24, 13.14) * mm, "end": v(-44.28, 13.06) * mm});
            skLineSegment(sketch, "E400", {"start": v(-44.28, 13.06) * mm, "end": v(-44.3, 12.97) * mm});
            skLineSegment(sketch, "E401", {"start": v(-44.3, 12.97) * mm, "end": v(-44.33, 12.85) * mm});
            skLineSegment(sketch, "E402", {"start": v(-44.33, 12.85) * mm, "end": v(-44.27, 12.63) * mm});
            skLineSegment(sketch, "E403", {"start": v(-44.27, 12.63) * mm, "end": v(-43.64, 11.51) * mm});
            skLineSegment(sketch, "E404", {"start": v(-43.64, 11.51) * mm, "end": v(-43.13, 10.34) * mm});
            skLineSegment(sketch, "E405", {"start": v(-43.13, 10.34) * mm, "end": v(-42.98, 10.16) * mm});
            skLineSegment(sketch, "E406", {"start": v(-42.98, 10.16) * mm, "end": v(-42.87, 10.1) * mm});
            skLineSegment(sketch, "E407", {"start": v(-42.87, 10.1) * mm, "end": v(-42.78, 10.08) * mm});
            skLineSegment(sketch, "E408", {"start": v(-42.78, 10.08) * mm, "end": v(-42.7, 10.06) * mm});
            skLineSegment(sketch, "E409", {"start": v(-42.7, 10.06) * mm, "end": v(-42.6, 10.05) * mm});
            skLineSegment(sketch, "E410", {"start": v(-42.6, 10.05) * mm, "end": v(-42.44, 10.05) * mm});
            skLineSegment(sketch, "E411", {"start": v(-42.44, 10.05) * mm, "end": v(-42.28, 10.07) * mm});
            skLineSegment(sketch, "E412", {"start": v(-42.28, 10.07) * mm, "end": v(-42.13, 10.1) * mm});
            skLineSegment(sketch, "E413", {"start": v(-42.13, 10.1) * mm, "end": v(-41.97, 10.13) * mm});
            skLineSegment(sketch, "E414", {"start": v(-41.97, 10.13) * mm, "end": v(-41.68, 10.23) * mm});
            skLineSegment(sketch, "E415", {"start": v(-41.68, 10.23) * mm, "end": v(-41.38, 10.33) * mm});
            skLineSegment(sketch, "E416", {"start": v(-41.38, 10.33) * mm, "end": v(-41.06, 10.37) * mm});
            skLineSegment(sketch, "E417", {"start": v(-41.06, 10.37) * mm, "end": v(-40.74, 10.37) * mm});
            skLineSegment(sketch, "E418", {"start": v(-40.74, 10.37) * mm, "end": v(-40.4, 10.36) * mm});
            skLineSegment(sketch, "E419", {"start": v(-40.4, 10.36) * mm, "end": v(-40.07, 10.32) * mm});
            skLineSegment(sketch, "E420", {"start": v(-40.07, 10.32) * mm, "end": v(-39.72, 10.27) * mm});
            skLineSegment(sketch, "E421", {"start": v(-39.72, 10.27) * mm, "end": v(-39.38, 10.2) * mm});
            skLineSegment(sketch, "E422", {"start": v(-39.38, 10.2) * mm, "end": v(-39.03, 10.1) * mm});
            skLineSegment(sketch, "E423", {"start": v(-39.03, 10.1) * mm, "end": v(-38.68, 10) * mm});
            skLineSegment(sketch, "E424", {"start": v(-38.68, 10) * mm, "end": v(-38.32, 9.87) * mm});
            skLineSegment(sketch, "E425", {"start": v(-38.32, 9.87) * mm, "end": v(-38.06, 9.77) * mm});
            skLineSegment(sketch, "E426", {"start": v(-38.06, 9.77) * mm, "end": v(-37.63, 6.99) * mm});
            skLineSegment(sketch, "E427", {"start": v(-37.63, 6.99) * mm, "end": v(-37.86, 6.8) * mm});
            skLineSegment(sketch, "E428", {"start": v(-37.86, 6.8) * mm, "end": v(-38.16, 6.59) * mm});
            skLineSegment(sketch, "E429", {"start": v(-38.16, 6.59) * mm, "end": v(-38.46, 6.38) * mm});
            skLineSegment(sketch, "E430", {"start": v(-38.46, 6.38) * mm, "end": v(-38.77, 6.19) * mm});
            skLineSegment(sketch, "E431", {"start": v(-38.77, 6.19) * mm, "end": v(-39.08, 6.02) * mm});
            skLineSegment(sketch, "E432", {"start": v(-39.08, 6.02) * mm, "end": v(-39.39, 5.86) * mm});
            skLineSegment(sketch, "E433", {"start": v(-39.39, 5.86) * mm, "end": v(-39.7, 5.73) * mm});
            skLineSegment(sketch, "E434", {"start": v(-39.7, 5.73) * mm, "end": v(-40.01, 5.61) * mm});
            skLineSegment(sketch, "E435", {"start": v(-40.01, 5.61) * mm, "end": v(-40.33, 5.52) * mm});
            skLineSegment(sketch, "E436", {"start": v(-40.33, 5.52) * mm, "end": v(-40.64, 5.46) * mm});
            skLineSegment(sketch, "E437", {"start": v(-40.64, 5.46) * mm, "end": v(-40.95, 5.47) * mm});
            skLineSegment(sketch, "E438", {"start": v(-40.95, 5.47) * mm, "end": v(-41.27, 5.48) * mm});
            skLineSegment(sketch, "E439", {"start": v(-41.27, 5.48) * mm, "end": v(-41.42, 5.47) * mm});
            skLineSegment(sketch, "E440", {"start": v(-41.42, 5.47) * mm, "end": v(-41.58, 5.45) * mm});
            skLineSegment(sketch, "E441", {"start": v(-41.58, 5.45) * mm, "end": v(-41.74, 5.42) * mm});
            skLineSegment(sketch, "E442", {"start": v(-41.74, 5.42) * mm, "end": v(-41.9, 5.36) * mm});
            skLineSegment(sketch, "E443", {"start": v(-41.9, 5.36) * mm, "end": v(-41.97, 5.33) * mm});
            skLineSegment(sketch, "E444", {"start": v(-41.97, 5.33) * mm, "end": v(-42.05, 5.29) * mm});
            skLineSegment(sketch, "E445", {"start": v(-42.05, 5.29) * mm, "end": v(-42.13, 5.23) * mm});
            skLineSegment(sketch, "E446", {"start": v(-42.13, 5.23) * mm, "end": v(-42.22, 5.15) * mm});
            skLineSegment(sketch, "E447", {"start": v(-42.22, 5.15) * mm, "end": v(-42.3, 4.94) * mm});
            skLineSegment(sketch, "E448", {"start": v(-42.3, 4.94) * mm, "end": v(-42.45, 3.66) * mm});
            skLineSegment(sketch, "E449", {"start": v(-42.45, 3.66) * mm, "end": v(-42.72, 2.41) * mm});
            skCircle(sketch, "E450", {"center": v(-55.12, 5.75) * mm, "radius": 15.11 * mm});
            skLineSegment(sketch, "E451", {"start": v(-42.28, -186.67) * mm, "end": v(-42.28, -189.71) * mm});
            skLineSegment(sketch, "E452", {"start": v(-42.28, -189.71) * mm, "end": v(-37.59, -191.42) * mm});
            skLineSegment(sketch, "E453", {"start": v(-37.59, -191.42) * mm, "end": v(-37.59, -194.53) * mm});
            skLineSegment(sketch, "E454", {"start": v(-37.59, -194.53) * mm, "end": v(-42.28, -196.24) * mm});
            skLineSegment(sketch, "E455", {"start": v(-42.28, -177.1) * mm, "end": v(-42.28, -180.14) * mm});
            skLineSegment(sketch, "E456", {"start": v(-42.28, -180.14) * mm, "end": v(-37.59, -181.85) * mm});
            skLineSegment(sketch, "E457", {"start": v(-37.59, -181.85) * mm, "end": v(-37.59, -184.96) * mm});
            skLineSegment(sketch, "E458", {"start": v(-37.59, -184.96) * mm, "end": v(-42.28, -186.67) * mm});
            skLineSegment(sketch, "E459", {"start": v(-42.28, -167.52) * mm, "end": v(-42.28, -170.57) * mm});
            skLineSegment(sketch, "E460", {"start": v(-42.28, -170.57) * mm, "end": v(-37.59, -172.27) * mm});
            skLineSegment(sketch, "E461", {"start": v(-37.59, -172.27) * mm, "end": v(-37.59, -175.39) * mm});
            skLineSegment(sketch, "E462", {"start": v(-37.59, -175.39) * mm, "end": v(-42.28, -177.1) * mm});
            skLineSegment(sketch, "E463", {"start": v(-42.28, -157.95) * mm, "end": v(-42.28, -161) * mm});
            skLineSegment(sketch, "E464", {"start": v(-42.28, -161) * mm, "end": v(-37.59, -162.7) * mm});
            skLineSegment(sketch, "E465", {"start": v(-37.59, -162.7) * mm, "end": v(-37.59, -165.82) * mm});
            skLineSegment(sketch, "E466", {"start": v(-37.59, -165.82) * mm, "end": v(-42.28, -167.52) * mm});
            skLineSegment(sketch, "E467", {"start": v(-42.28, -148.38) * mm, "end": v(-42.28, -151.42) * mm});
            skLineSegment(sketch, "E468", {"start": v(-42.28, -151.42) * mm, "end": v(-37.59, -153.13) * mm});
            skLineSegment(sketch, "E469", {"start": v(-37.59, -153.13) * mm, "end": v(-37.59, -156.24) * mm});
            skLineSegment(sketch, "E470", {"start": v(-37.59, -156.24) * mm, "end": v(-42.28, -157.95) * mm});
            skLineSegment(sketch, "E471", {"start": v(-42.28, -138.8) * mm, "end": v(-42.28, -141.85) * mm});
            skLineSegment(sketch, "E472", {"start": v(-42.28, -141.85) * mm, "end": v(-37.59, -143.56) * mm});
            skLineSegment(sketch, "E473", {"start": v(-37.59, -143.56) * mm, "end": v(-37.59, -146.67) * mm});
            skLineSegment(sketch, "E474", {"start": v(-37.59, -146.67) * mm, "end": v(-42.28, -148.38) * mm});
            skLineSegment(sketch, "E475", {"start": v(-42.28, -129.23) * mm, "end": v(-42.28, -132.28) * mm});
            skLineSegment(sketch, "E476", {"start": v(-42.28, -132.28) * mm, "end": v(-37.59, -133.98) * mm});
            skLineSegment(sketch, "E477", {"start": v(-37.59, -133.98) * mm, "end": v(-37.59, -137.1) * mm});
            skLineSegment(sketch, "E478", {"start": v(-37.59, -137.1) * mm, "end": v(-42.28, -138.8) * mm});
            skLineSegment(sketch, "E479", {"start": v(-42.28, -119.66) * mm, "end": v(-42.28, -122.7) * mm});
            skLineSegment(sketch, "E480", {"start": v(-42.28, -122.7) * mm, "end": v(-37.59, -124.41) * mm});
            skLineSegment(sketch, "E481", {"start": v(-37.59, -124.41) * mm, "end": v(-37.59, -127.53) * mm});
            skLineSegment(sketch, "E482", {"start": v(-37.59, -127.53) * mm, "end": v(-42.28, -129.23) * mm});
            skLineSegment(sketch, "E483", {"start": v(-42.28, -110.09) * mm, "end": v(-42.28, -113.13) * mm});
            skLineSegment(sketch, "E484", {"start": v(-42.28, -113.13) * mm, "end": v(-37.59, -114.84) * mm});
            skLineSegment(sketch, "E485", {"start": v(-37.59, -114.84) * mm, "end": v(-37.59, -117.95) * mm});
            skLineSegment(sketch, "E486", {"start": v(-37.59, -117.95) * mm, "end": v(-42.28, -119.66) * mm});
            skLineSegment(sketch, "E487", {"start": v(-42.28, -100.51) * mm, "end": v(-42.28, -103.56) * mm});
            skLineSegment(sketch, "E488", {"start": v(-42.28, -103.56) * mm, "end": v(-37.59, -105.27) * mm});
            skLineSegment(sketch, "E489", {"start": v(-37.59, -105.27) * mm, "end": v(-37.59, -108.38) * mm});
            skLineSegment(sketch, "E490", {"start": v(-37.59, -108.38) * mm, "end": v(-42.28, -110.09) * mm});
            skLineSegment(sketch, "E491", {"start": v(-42.28, -90.94) * mm, "end": v(-42.28, -93.99) * mm});
            skLineSegment(sketch, "E492", {"start": v(-42.28, -93.99) * mm, "end": v(-37.59, -95.7) * mm});
            skLineSegment(sketch, "E493", {"start": v(-37.59, -95.7) * mm, "end": v(-37.59, -98.8) * mm});
            skLineSegment(sketch, "E494", {"start": v(-37.59, -98.8) * mm, "end": v(-42.28, -100.51) * mm});
            skLineSegment(sketch, "E495", {"start": v(-42.28, -81.37) * mm, "end": v(-42.28, -84.41) * mm});
            skLineSegment(sketch, "E496", {"start": v(-42.28, -84.41) * mm, "end": v(-37.59, -86.12) * mm});
            skLineSegment(sketch, "E497", {"start": v(-37.59, -86.12) * mm, "end": v(-37.59, -89.23) * mm});
            skLineSegment(sketch, "E498", {"start": v(-37.59, -89.23) * mm, "end": v(-42.28, -90.94) * mm});
            skLineSegment(sketch, "E499", {"start": v(-42.28, -71.8) * mm, "end": v(-42.28, -74.84) * mm});
            skLineSegment(sketch, "E500", {"start": v(-42.28, -74.84) * mm, "end": v(-37.59, -76.55) * mm});
            skLineSegment(sketch, "E501", {"start": v(-37.59, -76.55) * mm, "end": v(-37.59, -79.66) * mm});
            skLineSegment(sketch, "E502", {"start": v(-37.59, -79.66) * mm, "end": v(-42.28, -81.37) * mm});
            skLineSegment(sketch, "E503", {"start": v(-42.28, -62.22) * mm, "end": v(-42.28, -65.27) * mm});
            skLineSegment(sketch, "E504", {"start": v(-42.28, -65.27) * mm, "end": v(-37.59, -66.97) * mm});
            skLineSegment(sketch, "E505", {"start": v(-37.59, -66.97) * mm, "end": v(-37.59, -70.09) * mm});
            skLineSegment(sketch, "E506", {"start": v(-37.59, -70.09) * mm, "end": v(-42.28, -71.8) * mm});
            skLineSegment(sketch, "E507", {"start": v(-42.28, -52.65) * mm, "end": v(-42.28, -55.7) * mm});
            skLineSegment(sketch, "E508", {"start": v(-42.28, -55.7) * mm, "end": v(-37.59, -57.4) * mm});
            skLineSegment(sketch, "E509", {"start": v(-37.59, -57.4) * mm, "end": v(-37.59, -60.52) * mm});
            skLineSegment(sketch, "E510", {"start": v(-37.59, -60.52) * mm, "end": v(-42.28, -62.22) * mm});
            skLineSegment(sketch, "E511", {"start": v(-42.28, -43.08) * mm, "end": v(-42.28, -46.12) * mm});
            skLineSegment(sketch, "E512", {"start": v(-42.28, -46.12) * mm, "end": v(-37.59, -47.83) * mm});
            skLineSegment(sketch, "E513", {"start": v(-37.59, -47.83) * mm, "end": v(-37.59, -50.94) * mm});
            skLineSegment(sketch, "E514", {"start": v(-37.59, -50.94) * mm, "end": v(-42.28, -52.65) * mm});
            skLineSegment(sketch, "E515", {"start": v(-42.28, -33.5) * mm, "end": v(-42.28, -36.55) * mm});
            skLineSegment(sketch, "E516", {"start": v(-42.28, -36.55) * mm, "end": v(-37.59, -38.26) * mm});
            skLineSegment(sketch, "E517", {"start": v(-37.59, -38.26) * mm, "end": v(-37.59, -41.37) * mm});
            skLineSegment(sketch, "E518", {"start": v(-37.59, -41.37) * mm, "end": v(-42.28, -43.08) * mm});
            skLineSegment(sketch, "E519", {"start": v(-42.28, -23.93) * mm, "end": v(-42.28, -26.98) * mm});
            skLineSegment(sketch, "E520", {"start": v(-42.28, -26.98) * mm, "end": v(-37.59, -28.68) * mm});
            skLineSegment(sketch, "E521", {"start": v(-37.59, -28.68) * mm, "end": v(-37.59, -31.8) * mm});
            skLineSegment(sketch, "E522", {"start": v(-37.59, -31.8) * mm, "end": v(-42.28, -33.5) * mm});
            skLineSegment(sketch, "E523", {"start": v(-42.28, -14.36) * mm, "end": v(-42.28, -17.4) * mm});
            skLineSegment(sketch, "E524", {"start": v(-42.28, -17.4) * mm, "end": v(-37.59, -19.11) * mm});
            skLineSegment(sketch, "E525", {"start": v(-37.59, -19.11) * mm, "end": v(-37.59, -22.23) * mm});
            skLineSegment(sketch, "E526", {"start": v(-37.59, -22.23) * mm, "end": v(-42.28, -23.93) * mm});
            skLineSegment(sketch, "E527", {"start": v(-42.28, -4.79) * mm, "end": v(-42.28, -7.83) * mm});
            skLineSegment(sketch, "E528", {"start": v(-42.28, -7.83) * mm, "end": v(-37.59, -9.54) * mm});
            skLineSegment(sketch, "E529", {"start": v(-37.59, -9.54) * mm, "end": v(-37.59, -12.65) * mm});
            skLineSegment(sketch, "E530", {"start": v(-37.59, -12.65) * mm, "end": v(-42.28, -14.36) * mm});
            skLineSegment(sketch, "E531", {"start": v(-42.28, 4.79) * mm, "end": v(-42.28, 1.74) * mm});
            skLineSegment(sketch, "E532", {"start": v(-42.28, 1.74) * mm, "end": v(-37.59, 0.04) * mm});
            skLineSegment(sketch, "E533", {"start": v(-37.59, 0.04) * mm, "end": v(-37.59, -3.08) * mm});
            skLineSegment(sketch, "E534", {"start": v(-37.59, -3.08) * mm, "end": v(-42.28, -4.79) * mm});
            skLineSegment(sketch, "E535", {"start": v(-42.28, 14.36) * mm, "end": v(-42.28, 11.31) * mm});
            skLineSegment(sketch, "E536", {"start": v(-42.28, 11.31) * mm, "end": v(-37.59, 9.6) * mm});
            skLineSegment(sketch, "E537", {"start": v(-37.59, 9.6) * mm, "end": v(-37.59, 6.5) * mm});
            skLineSegment(sketch, "E538", {"start": v(-37.59, 6.5) * mm, "end": v(-42.28, 4.79) * mm});
            skLineSegment(sketch, "E539", {"start": v(-42.28, 23.93) * mm, "end": v(-42.28, 20.89) * mm});
            skLineSegment(sketch, "E540", {"start": v(-42.28, 20.89) * mm, "end": v(-37.59, 19.18) * mm});
            skLineSegment(sketch, "E541", {"start": v(-37.59, 19.18) * mm, "end": v(-37.59, 16.07) * mm});
            skLineSegment(sketch, "E542", {"start": v(-37.59, 16.07) * mm, "end": v(-42.28, 14.36) * mm});
            skLineSegment(sketch, "E543", {"start": v(-42.28, 33.5) * mm, "end": v(-42.28, 30.46) * mm});
            skLineSegment(sketch, "E544", {"start": v(-42.28, 30.46) * mm, "end": v(-37.59, 28.75) * mm});
            skLineSegment(sketch, "E545", {"start": v(-37.59, 28.75) * mm, "end": v(-37.59, 25.64) * mm});
            skLineSegment(sketch, "E546", {"start": v(-37.59, 25.64) * mm, "end": v(-42.28, 23.93) * mm});
            skLineSegment(sketch, "E547", {"start": v(-42.28, 43.08) * mm, "end": v(-42.28, 40.03) * mm});
            skLineSegment(sketch, "E548", {"start": v(-42.28, 40.03) * mm, "end": v(-37.59, 38.33) * mm});
            skLineSegment(sketch, "E549", {"start": v(-37.59, 38.33) * mm, "end": v(-37.59, 35.21) * mm});
            skLineSegment(sketch, "E550", {"start": v(-37.59, 35.21) * mm, "end": v(-42.28, 33.5) * mm});
            skLineSegment(sketch, "E551", {"start": v(-42.28, 52.65) * mm, "end": v(-42.28, 49.6) * mm});
            skLineSegment(sketch, "E552", {"start": v(-42.28, 49.6) * mm, "end": v(-37.59, 47.9) * mm});
            skLineSegment(sketch, "E553", {"start": v(-37.59, 47.9) * mm, "end": v(-37.59, 44.78) * mm});
            skLineSegment(sketch, "E554", {"start": v(-37.59, 44.78) * mm, "end": v(-42.28, 43.08) * mm});
            skLineSegment(sketch, "E555", {"start": v(-42.28, 62.22) * mm, "end": v(-42.28, 59.18) * mm});
            skLineSegment(sketch, "E556", {"start": v(-42.28, 59.18) * mm, "end": v(-37.59, 57.47) * mm});
            skLineSegment(sketch, "E557", {"start": v(-37.59, 57.47) * mm, "end": v(-37.59, 54.36) * mm});
            skLineSegment(sketch, "E558", {"start": v(-37.59, 54.36) * mm, "end": v(-42.28, 52.65) * mm});
            skLineSegment(sketch, "E559", {"start": v(-42.28, 71.8) * mm, "end": v(-42.28, 68.75) * mm});
            skLineSegment(sketch, "E560", {"start": v(-42.28, 68.75) * mm, "end": v(-37.59, 67.04) * mm});
            skLineSegment(sketch, "E561", {"start": v(-37.59, 67.04) * mm, "end": v(-37.59, 63.93) * mm});
            skLineSegment(sketch, "E562", {"start": v(-37.59, 63.93) * mm, "end": v(-42.28, 62.22) * mm});
            skLineSegment(sketch, "E563", {"start": v(-42.28, 81.37) * mm, "end": v(-42.28, 78.32) * mm});
            skLineSegment(sketch, "E564", {"start": v(-42.28, 78.32) * mm, "end": v(-37.59, 76.62) * mm});
            skLineSegment(sketch, "E565", {"start": v(-37.59, 76.62) * mm, "end": v(-37.59, 73.5) * mm});
            skLineSegment(sketch, "E566", {"start": v(-37.59, 73.5) * mm, "end": v(-42.28, 71.8) * mm});
            skLineSegment(sketch, "E567", {"start": v(-42.28, 90.94) * mm, "end": v(-42.28, 87.9) * mm});
            skLineSegment(sketch, "E568", {"start": v(-42.28, 87.9) * mm, "end": v(-37.59, 86.2) * mm});
            skLineSegment(sketch, "E569", {"start": v(-37.59, 86.2) * mm, "end": v(-37.59, 83.08) * mm});
            skLineSegment(sketch, "E570", {"start": v(-37.59, 83.08) * mm, "end": v(-42.28, 81.37) * mm});
            skLineSegment(sketch, "E571", {"start": v(-42.28, 100.51) * mm, "end": v(-42.28, 97.47) * mm});
            skLineSegment(sketch, "E572", {"start": v(-42.28, 97.47) * mm, "end": v(-37.59, 95.76) * mm});
            skLineSegment(sketch, "E573", {"start": v(-37.59, 95.76) * mm, "end": v(-37.59, 92.65) * mm});
            skLineSegment(sketch, "E574", {"start": v(-37.59, 92.65) * mm, "end": v(-42.28, 90.94) * mm});
            skLineSegment(sketch, "E575", {"start": v(-42.28, 110.09) * mm, "end": v(-42.28, 107.04) * mm});
            skLineSegment(sketch, "E576", {"start": v(-42.28, 107.04) * mm, "end": v(-37.59, 105.34) * mm});
            skLineSegment(sketch, "E577", {"start": v(-37.59, 105.34) * mm, "end": v(-37.59, 102.22) * mm});
            skLineSegment(sketch, "E578", {"start": v(-37.59, 102.22) * mm, "end": v(-42.28, 100.51) * mm});
            skLineSegment(sketch, "E579", {"start": v(-42.28, 119.66) * mm, "end": v(-42.28, 116.62) * mm});
            skLineSegment(sketch, "E580", {"start": v(-42.28, 116.62) * mm, "end": v(-37.59, 114.9) * mm});
            skLineSegment(sketch, "E581", {"start": v(-37.59, 114.9) * mm, "end": v(-37.59, 111.8) * mm});
            skLineSegment(sketch, "E582", {"start": v(-37.59, 111.8) * mm, "end": v(-42.28, 110.09) * mm});
            skLineSegment(sketch, "E583", {"start": v(-42.28, 129.23) * mm, "end": v(-42.28, 126.19) * mm});
            skLineSegment(sketch, "E584", {"start": v(-42.28, 126.19) * mm, "end": v(-37.59, 124.48) * mm});
            skLineSegment(sketch, "E585", {"start": v(-37.59, 124.48) * mm, "end": v(-37.59, 121.37) * mm});
            skLineSegment(sketch, "E586", {"start": v(-37.59, 121.37) * mm, "end": v(-42.28, 119.66) * mm});
            skLineSegment(sketch, "E587", {"start": v(-42.28, 138.8) * mm, "end": v(-42.28, 135.76) * mm});
            skLineSegment(sketch, "E588", {"start": v(-42.28, 135.76) * mm, "end": v(-37.59, 134.05) * mm});
            skLineSegment(sketch, "E589", {"start": v(-37.59, 134.05) * mm, "end": v(-37.59, 130.94) * mm});
            skLineSegment(sketch, "E590", {"start": v(-37.59, 130.94) * mm, "end": v(-42.28, 129.23) * mm});
            skLineSegment(sketch, "E591", {"start": v(-42.28, 148.38) * mm, "end": v(-42.28, 145.33) * mm});
            skLineSegment(sketch, "E592", {"start": v(-42.28, 145.33) * mm, "end": v(-37.59, 143.63) * mm});
            skLineSegment(sketch, "E593", {"start": v(-37.59, 143.63) * mm, "end": v(-37.59, 140.51) * mm});
            skLineSegment(sketch, "E594", {"start": v(-37.59, 140.51) * mm, "end": v(-42.28, 138.8) * mm});
            skLineSegment(sketch, "E595", {"start": v(-42.28, 157.95) * mm, "end": v(-42.28, 154.9) * mm});
            skLineSegment(sketch, "E596", {"start": v(-42.28, 154.9) * mm, "end": v(-37.59, 153.2) * mm});
            skLineSegment(sketch, "E597", {"start": v(-37.59, 153.2) * mm, "end": v(-37.59, 150.08) * mm});
            skLineSegment(sketch, "E598", {"start": v(-37.59, 150.08) * mm, "end": v(-42.28, 148.38) * mm});
            skLineSegment(sketch, "E599", {"start": v(-42.28, 167.52) * mm, "end": v(-42.28, 164.48) * mm});
            skLineSegment(sketch, "E600", {"start": v(-42.28, 164.48) * mm, "end": v(-37.59, 162.77) * mm});
            skLineSegment(sketch, "E601", {"start": v(-37.59, 162.77) * mm, "end": v(-37.59, 159.66) * mm});
            skLineSegment(sketch, "E602", {"start": v(-37.59, 159.66) * mm, "end": v(-42.28, 157.95) * mm});
            skLineSegment(sketch, "E603", {"start": v(-42.28, 177.1) * mm, "end": v(-42.28, 174.05) * mm});
            skLineSegment(sketch, "E604", {"start": v(-42.28, 174.05) * mm, "end": v(-37.59, 172.35) * mm});
            skLineSegment(sketch, "E605", {"start": v(-37.59, 172.35) * mm, "end": v(-37.59, 169.23) * mm});
            skLineSegment(sketch, "E606", {"start": v(-37.59, 169.23) * mm, "end": v(-42.28, 167.52) * mm});
            skLineSegment(sketch, "E607", {"start": v(-42.28, 186.67) * mm, "end": v(-42.28, 183.62) * mm});
            skLineSegment(sketch, "E608", {"start": v(-42.28, 183.62) * mm, "end": v(-37.59, 181.92) * mm});
            skLineSegment(sketch, "E609", {"start": v(-37.59, 181.92) * mm, "end": v(-37.59, 178.8) * mm});
            skLineSegment(sketch, "E610", {"start": v(-37.59, 178.8) * mm, "end": v(-42.28, 177.1) * mm});
            skLineSegment(sketch, "E611", {"start": v(-42.28, 196.24) * mm, "end": v(-42.28, 193.2) * mm});
            skLineSegment(sketch, "E612", {"start": v(-42.28, 193.2) * mm, "end": v(-37.59, 191.5) * mm});
            skLineSegment(sketch, "E613", {"start": v(-37.59, 191.5) * mm, "end": v(-37.59, 188.38) * mm});
            skLineSegment(sketch, "E614", {"start": v(-37.59, 188.38) * mm, "end": v(-42.28, 186.67) * mm});
            skLineSegment(sketch, "E615", {"start": v(-30.23, 75.6) * mm, "end": v(-30.23, 5.75) * mm});
            skLineSegment(sketch, "E616", {"start": v(-55.12, 5.75) * mm, "end": v(-30.23, 5.75) * mm});
            skLineSegment(sketch, "E617", {"start": v(-30.23, 5.75) * mm, "end": v(-30.23, -64.1) * mm});
            skLineSegment(sketch, "E618", {"start": v(-37.59, 73.5) * mm, "end": v(-30.23, 73.5) * mm});
            skLineSegment(sketch, "E619", {"start": v(-37.59, -66.97) * mm, "end": v(-30.23, -66.97) * mm});
            skLineSegment(sketch, "E620", {"start": v(-30.23, -66.97) * mm, "end": v(-30.23, -64.1) * mm});
            skSolve(sketch);
        }
        {
            var Q0;
            {var subQ0=sQuery(id+"F0.wireOp",EDGE,"E537");Q0=makeQuery(id+"F0.imprint","IMPRINT",FACE,{"disambiguationData":[TD([[makeQuery(id+"F0.imprint","IMPRINT",EDGE,{"derivedFrom":subQ0}),1.0]])]});}
            var Q1;
            Q1=makeQuery(id+"F0.imprint","IMPRINT",FACE,{"disambiguationData":[TD([[makeQuery(id+"F0.imprint","IMPRINT",EDGE,{"derivedFrom":sQuery(id+"F0.wireOp",EDGE,"E503")}),1.0]])]});
            var Q2;
            {var subQ1=sQuery(id+"F0.wireOp",EDGE,"E531");var subQ3=sQuery(id+"F0.wireOp",EDGE,"E6");var subQ4=makeQuery(id+"F0.imprint","INTERSECT",VERTEX,{"derivedFrom":[subQ3,subQ1]});Q2=makeQuery(id+"F0.imprint","IMPRINT",FACE,{"disambiguationData":[TD([[makeQuery(id+"F0.imprint","IMPRINT",EDGE,{"disambiguationData":[TD([[subQ4,-1.0]])],"derivedFrom":subQ3}),1.0]])]});}
            var Q3;
            {var subQ0=sQuery(id+"F0.wireOp",EDGE,"E535");var subQ1=sQuery(id+"F0.wireOp",EDGE,"E450");var subQ2=makeQuery(id+"F0.imprint","INTERSECT",VERTEX,{"derivedFrom":[subQ1,subQ0]});Q3=makeQuery(id+"F0.imprint","IMPRINT",FACE,{"disambiguationData":[TD([[makeQuery(id+"F0.imprint","IMPRINT",EDGE,{"disambiguationData":[TD([[subQ2,-1.0]])],"derivedFrom":subQ1}),-1.0]])]});}
            extrude(context, id + "F1", {"entities" : qUnion([Q0, Q1, Q2, Q3]), "depth" : 19.05 * mm, "offsetDistance" : 25.4 * mm});
        }
        {
            var Q0;
            Q0=makeQuery(id+"F1.opExtrude","SWEPT_FACE",FACE,{"disambiguationData":[OSD([sQuery(id+"F0.wireOp",EDGE,"E618")])]});
            var sketch = newSketch(context, id + "F2", { "sketchPlane" : qUnion([Q0])});
            skLineSegment(sketch, "E621.1", {"start": v(-30.23, -19.05) * mm, "end": v(-30.23, -9.53) * mm});
            skLineSegment(sketch, "E622", {"start": v(-30.23, -9.53) * mm, "end": v(-30.23, 0) * mm});
            skCircle(sketch, "E623", {"center": v(-30.23, -9.53) * mm, "radius": 6.35 * mm});
            skArc(sketch, "E624", {"start": v(-30.23, -19.05) * mm, "mid": v(-20.7, -9.53) * mm, "end": v(-30.23, 0) * mm});
            skLineSegment(sketch, "E625", {"start": v(-30.23, -12.45) * mm, "end": v(-42.28, -12.45) * mm});
            skLineSegment(sketch, "E626.0", {"start": v(-42.28, -19.05) * mm, "end": v(-42.28, 0) * mm});
            skLineSegment(sketch, "E627", {"start": v(-37.2, -12.45) * mm, "end": v(-37.2, -15.5) * mm});
            skLineSegment(sketch, "E628", {"start": v(-37.2, -15.5) * mm, "end": v(-42.28, -15.5) * mm});
            skSolve(sketch);
        }
        {
            var Q0;
            {var subQ0=sQuery(id+"F2.wireOp",EDGE,"E624");Q0=makeQuery(id+"F2.imprint","IMPRINT",FACE,{"disambiguationData":[TD([[makeQuery(id+"F2.imprint","IMPRINT",EDGE,{"derivedFrom":subQ0}),1.0]])]});}
            var Q1;
            Q1=makeQuery(id+"F1.opExtrude","SWEPT_FACE",FACE,{"disambiguationData":[OSD([sQuery(id+"F0.wireOp",EDGE,"E619")])]});
            extrude(context, id + "F3", {"entities" : qUnion([Q0]), "operationType" : NewBodyOperationType.ADD, "endBound" : BoundingType.UP_TO_SURFACE, "oppositeDirection" : true, "depth" : 140.97 * mm, "endBoundEntityFace" : qUnion([Q1]), "offsetDistance" : 25.4 * mm});
        }
        {
            var Q0;
            {var subQ0=sQuery(id+"F2.wireOp",EDGE,"E622");var subQ1=sQuery(id+"F2.wireOp",EDGE,"E621.1");var subQ2=makeQuery(id+"F2.imprint","INTERSECT",VERTEX,{"derivedFrom":[subQ1,subQ0]});Q0=makeQuery(id+"F2.imprint","IMPRINT",FACE,{"disambiguationData":[TD([[makeQuery(id+"F2.imprint","IMPRINT",EDGE,{"disambiguationData":[TD([[subQ2,1.0]])],"derivedFrom":subQ1}),1.0]])]});}
            var Q1;
            {var subQ0=sQuery(id+"F2.wireOp",EDGE,"E625");var subQ1=sQuery(id+"F2.wireOp",EDGE,"E621.1");var subQ2=makeQuery(id+"F2.imprint","INTERSECT",VERTEX,{"derivedFrom":[subQ1,subQ0]});Q1=makeQuery(id+"F2.imprint","IMPRINT",FACE,{"disambiguationData":[TD([[makeQuery(id+"F2.imprint","IMPRINT",EDGE,{"disambiguationData":[TD([[subQ2,1.0]])],"derivedFrom":subQ1}),1.0]])]});}
            extrude(context, id + "F4", {"entities" : qUnion([Q0, Q1]), "operationType" : NewBodyOperationType.REMOVE, "oppositeDirection" : true, "depth" : 142.24 * mm, "offsetDistance" : 25.4 * mm});
        }
        {
            var Q0;
            Q0=makeQuery(id+"F0.imprint","IMPRINT",FACE,{"disambiguationData":[TD([[makeQuery(id+"F0.imprint","IMPRINT",EDGE,{"derivedFrom":sQuery(id+"F0.wireOp",EDGE,"E0")}),-1.0]])]});
            var Q1;
            {var subQ5=sQuery(id+"F0.wireOp",EDGE,"E374");Q1=makeQuery(id+"F0.imprint","IMPRINT",FACE,{"disambiguationData":[TD([[makeQuery(id+"F0.imprint","IMPRINT",EDGE,{"derivedFrom":subQ5}),-1.0]])]});}
            var Q2;
            {var subQ0=sQuery(id+"F0.wireOp",EDGE,"E419");Q2=makeQuery(id+"F0.imprint","IMPRINT",FACE,{"disambiguationData":[TD([[makeQuery(id+"F0.imprint","IMPRINT",EDGE,{"derivedFrom":subQ0}),-1.0]])]});}
            var Q3;
            {var subQ0=sQuery(id+"F0.wireOp",EDGE,"E14");Q3=makeQuery(id+"F0.imprint","IMPRINT",FACE,{"disambiguationData":[TD([[makeQuery(id+"F0.imprint","IMPRINT",EDGE,{"derivedFrom":subQ0}),-1.0]])]});}
            var Q4;
            {var subQ0=sQuery(id+"F0.wireOp",EDGE,"E59");Q4=makeQuery(id+"F0.imprint","IMPRINT",FACE,{"disambiguationData":[TD([[makeQuery(id+"F0.imprint","IMPRINT",EDGE,{"derivedFrom":subQ0}),-1.0]])]});}
            var Q5;
            {var subQ0=sQuery(id+"F0.wireOp",EDGE,"E104");Q5=makeQuery(id+"F0.imprint","IMPRINT",FACE,{"disambiguationData":[TD([[makeQuery(id+"F0.imprint","IMPRINT",EDGE,{"derivedFrom":subQ0}),-1.0]])]});}
            var Q6;
            {var subQ5=sQuery(id+"F0.wireOp",EDGE,"E149");Q6=makeQuery(id+"F0.imprint","IMPRINT",FACE,{"disambiguationData":[TD([[makeQuery(id+"F0.imprint","IMPRINT",EDGE,{"derivedFrom":subQ5}),-1.0]])]});}
            var Q7;
            {var subQ5=sQuery(id+"F0.wireOp",EDGE,"E194");Q7=makeQuery(id+"F0.imprint","IMPRINT",FACE,{"disambiguationData":[TD([[makeQuery(id+"F0.imprint","IMPRINT",EDGE,{"derivedFrom":subQ5}),-1.0]])]});}
            var Q8;
            {var subQ5=sQuery(id+"F0.wireOp",EDGE,"E239");Q8=makeQuery(id+"F0.imprint","IMPRINT",FACE,{"disambiguationData":[TD([[makeQuery(id+"F0.imprint","IMPRINT",EDGE,{"derivedFrom":subQ5}),-1.0]])]});}
            var Q9;
            {var subQ5=sQuery(id+"F0.wireOp",EDGE,"E284");Q9=makeQuery(id+"F0.imprint","IMPRINT",FACE,{"disambiguationData":[TD([[makeQuery(id+"F0.imprint","IMPRINT",EDGE,{"derivedFrom":subQ5}),-1.0]])]});}
            var Q10;
            {var subQ5=sQuery(id+"F0.wireOp",EDGE,"E329");Q10=makeQuery(id+"F0.imprint","IMPRINT",FACE,{"disambiguationData":[TD([[makeQuery(id+"F0.imprint","IMPRINT",EDGE,{"derivedFrom":subQ5}),-1.0]])]});}
            var Q11;
            {var subQ0=sQuery(id+"F0.wireOp",EDGE,"E434");var subQ1=sQuery(id+"F0.wireOp",EDGE,"E433");var subQ2=makeQuery(id+"F0.imprint","INTERSECT",VERTEX,{"derivedFrom":[subQ1,subQ0]});Q11=makeQuery(id+"F0.imprint","IMPRINT",FACE,{"disambiguationData":[TD([[makeQuery(id+"F0.imprint","IMPRINT",EDGE,{"disambiguationData":[TD([[subQ2,1.0]])],"derivedFrom":subQ1}),-1.0]])]});}
            extrude(context, id + "F5", {"entities" : qUnion([Q0, Q1, Q2, Q3, Q4, Q5, Q6, Q7, Q8, Q9, Q10, Q11]), "depth" : 12.7 * mm, "offsetDistance" : 25.4 * mm});
        }
        {
            var Q0;
            {var subQ5=sQuery(id+"F0.wireOp",EDGE,"E374");Q0=makeQuery(id+"F0.imprint","IMPRINT",FACE,{"disambiguationData":[TD([[makeQuery(id+"F0.imprint","IMPRINT",EDGE,{"derivedFrom":subQ5}),-1.0]])]});}
            var Q1;
            {var subQ5=sQuery(id+"F0.wireOp",EDGE,"E329");Q1=makeQuery(id+"F0.imprint","IMPRINT",FACE,{"disambiguationData":[TD([[makeQuery(id+"F0.imprint","IMPRINT",EDGE,{"derivedFrom":subQ5}),-1.0]])]});}
            var Q2;
            {var subQ5=sQuery(id+"F0.wireOp",EDGE,"E284");Q2=makeQuery(id+"F0.imprint","IMPRINT",FACE,{"disambiguationData":[TD([[makeQuery(id+"F0.imprint","IMPRINT",EDGE,{"derivedFrom":subQ5}),-1.0]])]});}
            var Q3;
            {var subQ5=sQuery(id+"F0.wireOp",EDGE,"E239");Q3=makeQuery(id+"F0.imprint","IMPRINT",FACE,{"disambiguationData":[TD([[makeQuery(id+"F0.imprint","IMPRINT",EDGE,{"derivedFrom":subQ5}),-1.0]])]});}
            var Q4;
            {var subQ5=sQuery(id+"F0.wireOp",EDGE,"E194");Q4=makeQuery(id+"F0.imprint","IMPRINT",FACE,{"disambiguationData":[TD([[makeQuery(id+"F0.imprint","IMPRINT",EDGE,{"derivedFrom":subQ5}),-1.0]])]});}
            var Q5;
            {var subQ0=sQuery(id+"F0.wireOp",EDGE,"E419");Q5=makeQuery(id+"F0.imprint","IMPRINT",FACE,{"disambiguationData":[TD([[makeQuery(id+"F0.imprint","IMPRINT",EDGE,{"derivedFrom":subQ0}),-1.0]])]});}
            var Q6;
            {var subQ0=sQuery(id+"F0.wireOp",EDGE,"E14");Q6=makeQuery(id+"F0.imprint","IMPRINT",FACE,{"disambiguationData":[TD([[makeQuery(id+"F0.imprint","IMPRINT",EDGE,{"derivedFrom":subQ0}),-1.0]])]});}
            var Q7;
            {var subQ0=sQuery(id+"F0.wireOp",EDGE,"E59");Q7=makeQuery(id+"F0.imprint","IMPRINT",FACE,{"disambiguationData":[TD([[makeQuery(id+"F0.imprint","IMPRINT",EDGE,{"derivedFrom":subQ0}),-1.0]])]});}
            var Q8;
            {var subQ0=sQuery(id+"F0.wireOp",EDGE,"E104");Q8=makeQuery(id+"F0.imprint","IMPRINT",FACE,{"disambiguationData":[TD([[makeQuery(id+"F0.imprint","IMPRINT",EDGE,{"derivedFrom":subQ0}),-1.0]])]});}
            var Q9;
            {var subQ5=sQuery(id+"F0.wireOp",EDGE,"E149");Q9=makeQuery(id+"F0.imprint","IMPRINT",FACE,{"disambiguationData":[TD([[makeQuery(id+"F0.imprint","IMPRINT",EDGE,{"derivedFrom":subQ5}),-1.0]])]});}
            extrude(context, id + "F6", {"entities" : qUnion([Q0, Q1, Q2, Q3, Q4, Q5, Q6, Q7, Q8, Q9]), "operationType" : NewBodyOperationType.ADD, "depth" : 18.8 * mm, "offsetDistance" : 25.4 * mm});
        }
        {
            var Q0;
            Q0=makeQuery(id+"F0.imprint","IMPRINT",FACE,{"disambiguationData":[TD([[makeQuery(id+"F0.imprint","IMPRINT",EDGE,{"derivedFrom":sQuery(id+"F0.wireOp",EDGE,"E0")}),-1.0]])]});
            var sketch = newSketch(context, id + "F7", { "sketchPlane" : qUnion([Q0])});
            skPoint(sketch, "E629.0", {"position": v(-55.12, 5.75) * mm});
            skCircle(sketch, "E630", {"center": v(-55.12, 5.75) * mm, "radius": 6.35 * mm});
            skSolve(sketch);
        }
        {
            var Q0;
            Q0=makeQuery(id+"F7.imprint","IMPRINT",FACE,{"disambiguationData":[TD([[makeQuery(id+"F7.imprint","IMPRINT",EDGE,{"derivedFrom":sQuery(id+"F7.wireOp",EDGE,"E630")}),1.0]])]});
            extrude(context, id + "F8", {"entities" : qUnion([Q0]), "operationType" : NewBodyOperationType.REMOVE, "depth" : 25.4 * mm, "offsetDistance" : 25.4 * mm});
        }
        {
            var Q0;
            {var subQ0=sQuery(id+"F2.wireOp",EDGE,"E626.0");var subQ1=sQuery(id+"F2.wireOp",EDGE,"E625");var subQ2=makeQuery(id+"F2.imprint","INTERSECT",VERTEX,{"derivedFrom":[subQ1,subQ0]});Q0=makeQuery(id+"F2.imprint","IMPRINT",FACE,{"disambiguationData":[TD([[makeQuery(id+"F2.imprint","IMPRINT",EDGE,{"disambiguationData":[TD([[subQ2,1.0]])],"derivedFrom":subQ0}),-1.0]])]});}
            var Q1;
            {var subQ0=sQuery(id+"F2.wireOp",EDGE,"E627");Q1=makeQuery(id+"F2.imprint","IMPRINT",FACE,{"disambiguationData":[TD([[makeQuery(id+"F2.imprint","IMPRINT",EDGE,{"derivedFrom":subQ0}),-1.0]])]});}
            var Q2;
            {var subQ0=sQuery(id+"F0.wireOp",EDGE,"E619");Q2=makeQuery(id+"F3.boolean.opBoolean","MERGE",FACE,{"derivedFrom":[makeQuery(id+"F1.opExtrude","SWEPT_FACE",FACE,{"disambiguationData":[OSD([subQ0])]}),makeQuery(id+"F3.opExtrude","CAP_FACE",FACE,{"disambiguationData":[OSD([subQ0])],"isStart":false})]});}
            extrude(context, id + "F9", {"entities" : qUnion([Q0, Q1]), "operationType" : NewBodyOperationType.REMOVE, "endBound" : BoundingType.UP_TO_SURFACE, "oppositeDirection" : true, "depth" : 25.4 * mm, "endBoundEntityFace" : qUnion([Q2]), "offsetDistance" : 25.4 * mm});
        }
    });
